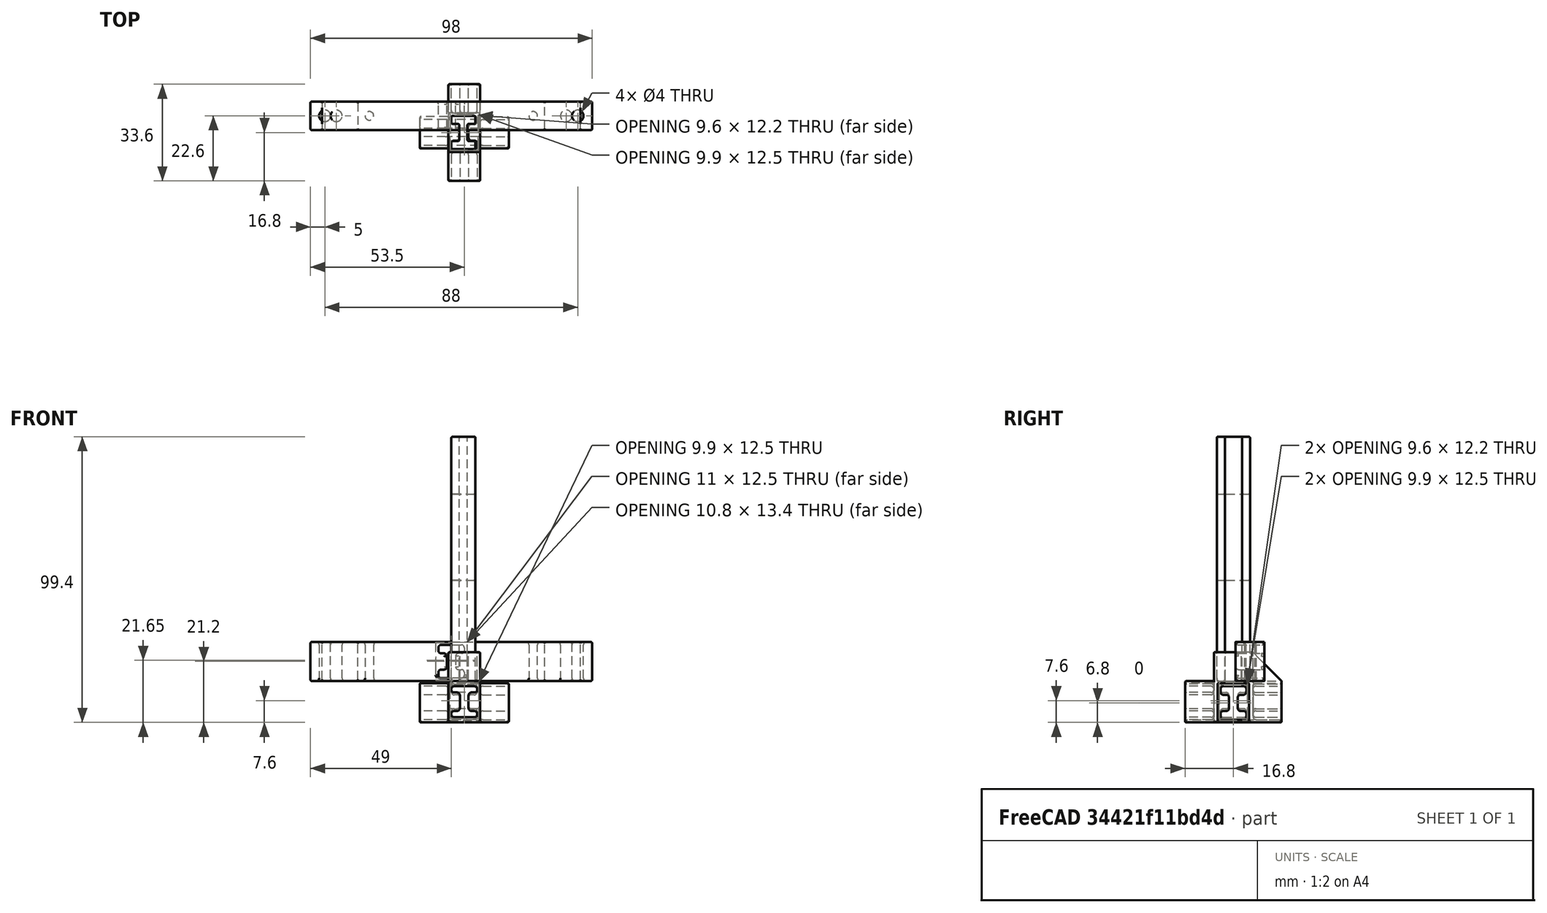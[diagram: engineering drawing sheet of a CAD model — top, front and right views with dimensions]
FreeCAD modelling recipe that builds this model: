
FCSTD DOCUMENT  (FreeCAD 1.2R20260106 (Git shallow))
Label: Joints
License: All rights reserved
LicenseURL: https://en.wikipedia.org/wiki/All_rights_reserved
objects: PartDesign::Fillet×30, Sketcher::SketchObject×28, PartDesign::Pad×25, App::Point×17, PartDesign::SubShapeBinder×10, PartDesign::Body×10, PartDesign::Pocket×6, PartDesign::Hole×3
note: 268 computed .brp shape members not serialized (recipe doc carries the construction recipe); baked Part::Feature solids carry a one-line shape summary decoded from their .brp

FEATURE [Sketcher::SketchObject] Sketch  label="MasterSketchConnector"
  ArcFitTolerance = 1e-06
  ExternalTypes = [0]
  FullyConstrained = true
  MakeInternals = false
  MapMode = 5
  expr: Constraints[20] = 3 * 3
  expr: Constraints[39] = 3 / 2
  expr: Constraints[79] = 2.8 * 2
  sketch-geometry (41):
    g0: LineSegment [constr] StartX=0 StartY=0 StartZ=0 EndX=0 EndY=-3 EndZ=0
    g1: LineSegment [constr] StartX=0 StartY=-3 StartZ=0 EndX=9 EndY=-3 EndZ=0
    g2: LineSegment [constr] StartX=9 StartY=-3 StartZ=0 EndX=9 EndY=0 EndZ=0
    g3: LineSegment [constr] StartX=9 StartY=0 StartZ=0 EndX=0 EndY=0 EndZ=0
    g4: GeomPoint [constr] X=4.5 Y=-1.5 Z=0
    g5: LineSegment [constr] StartX=0 StartY=-8.6 StartZ=0 EndX=0 EndY=-11.6 EndZ=0
    g6: LineSegment [constr] StartX=0 StartY=-11.6 StartZ=0 EndX=9 EndY=-11.6 EndZ=0
    g7: LineSegment [constr] StartX=9 StartY=-11.6 StartZ=0 EndX=9 EndY=-8.6 EndZ=0
    g8: LineSegment [constr] StartX=9 StartY=-8.6 StartZ=0 EndX=0 EndY=-8.6 EndZ=0
    g9: GeomPoint [constr] X=4.5 Y=-10.1 Z=0
    g10: LineSegment [constr] StartX=4.5 StartY=-1.5 StartZ=0 EndX=4.5 EndY=-10.1 EndZ=0
    g11: GeomPoint [constr] X=4.5 Y=-3 Z=0
    g12: GeomPoint [constr] X=4.5 Y=-8.6 Z=0
    g13: LineSegment [constr] StartX=4.5 StartY=-3 StartZ=0 EndX=4.5 EndY=-8.6 EndZ=0
    g14: LineSegment [constr] StartX=4.5 StartY=-8.6 StartZ=0 EndX=6 EndY=-8.6 EndZ=0
    g15: LineSegment [constr] StartX=6 StartY=-8.6 StartZ=0 EndX=6 EndY=-3 EndZ=0
    g16: LineSegment [constr] StartX=6 StartY=-3 StartZ=0 EndX=4.5 EndY=-3 EndZ=0
    g17: LineSegment [constr] StartX=4.5 StartY=-3 StartZ=0 EndX=3 EndY=-3 EndZ=0
    g18: LineSegment [constr] StartX=3 StartY=-3 StartZ=0 EndX=3 EndY=-8.6 EndZ=0
    g19: LineSegment [constr] StartX=3 StartY=-8.6 StartZ=0 EndX=4.5 EndY=-8.6 EndZ=0
    g20: LineSegment [constr] StartX=4.5 StartY=-8.6 StartZ=0 EndX=4.5 EndY=-3 EndZ=0
    g21: LineSegment [constr] StartX=0 StartY=0 StartZ=0 EndX=9 EndY=0 EndZ=0
    g22: LineSegment [constr] StartX=9 StartY=0 StartZ=0 EndX=9 EndY=-3 EndZ=0
    g23: LineSegment StartX=0 StartY=0 StartZ=0 EndX=9 EndY=0 EndZ=0
    g24: LineSegment StartX=9 StartY=0 StartZ=0 EndX=9 EndY=-3 EndZ=0
    g25: LineSegment StartX=9 StartY=-3 StartZ=0 EndX=6 EndY=-3 EndZ=0
    g26: LineSegment StartX=6 StartY=-3 StartZ=0 EndX=6 EndY=-8.6 EndZ=0
    g27: LineSegment StartX=6 StartY=-8.6 StartZ=0 EndX=9 EndY=-8.6 EndZ=0
    g28: LineSegment StartX=9 StartY=-8.6 StartZ=0 EndX=9 EndY=-11.6 EndZ=0
    g29: LineSegment StartX=9 StartY=-11.6 StartZ=0 EndX=0 EndY=-11.6 EndZ=0
    g30: LineSegment StartX=0 StartY=-11.6 StartZ=0 EndX=0 EndY=-8.6 EndZ=0
    g31: LineSegment StartX=0 StartY=-8.6 StartZ=0 EndX=3 EndY=-8.6 EndZ=0
    g32: LineSegment StartX=3 StartY=-8.6 StartZ=0 EndX=3 EndY=-3 EndZ=0
    g33: LineSegment StartX=3 StartY=-3 StartZ=0 EndX=0 EndY=-3 EndZ=0
    g34: LineSegment StartX=0 StartY=-3 StartZ=0 EndX=0 EndY=0 EndZ=0
    g35: GeomPoint X=4.5 Y=-5.8 Z=0
    g36: LineSegment StartX=-1 StartY=-12.6 StartZ=0 EndX=10 EndY=-12.6 EndZ=0
    g37: LineSegment StartX=10 StartY=-12.6 StartZ=0 EndX=10 EndY=1 EndZ=0
    g38: LineSegment StartX=10 StartY=1 StartZ=0 EndX=-1 EndY=1 EndZ=0
    g39: LineSegment StartX=-1 StartY=1 StartZ=0 EndX=-1 EndY=-12.6 EndZ=0
    g40: GeomPoint [constr] X=4.5 Y=-5.8 Z=0
  constraints (94):
    c: Coincident(g0,g1)
    c: Coincident(g1,g2)
    c: Coincident(g2,g3)
    c: Coincident(g3,g0)
    c: Vertical(g0)
    c: Vertical(g2)
    c: Horizontal(g1)
    c: Horizontal(g3)
    c: Symmetric(g0,g2,g4)
    c: Coincident(g5,g6)
    c: Coincident(g6,g7)
    c: Coincident(g7,g8)
    c: Coincident(g8,g5)
    c: Vertical(g5)
    c: Vertical(g7)
    c: Horizontal(g6)
    c: Horizontal(g8)
    c: Equal(g8,g1)
    c: Equal(g7,g2)
    c: Symmetric(g5,g7,g9)
    c: DistanceX(g3,g3) = 9
    c: DistanceY(g0,g0) = 3
    c: Coincident(g0,g-1)
    c: PointOnObject(g5,g-2)
    c: Coincident(g10,g4)
    c: Coincident(g10,g9)
    c: PointOnObject(g11,g10)
    c: PointOnObject(g12,g10)
    c: PointOnObject(g11,g1)
    c: PointOnObject(g12,g8)
    c: Coincident(g13,g14)
    c: Coincident(g14,g15)
    c: Coincident(g15,g16)
    c: Coincident(g16,g13)
    c: Vertical(g13)
    c: Vertical(g15)
    c: Horizontal(g14)
    c: Horizontal(g16)
    c: Coincident(g13,g11)
    c: Distance(g14,g14) = 1.5
    c: Coincident(g17,g18)
    c: Coincident(g18,g19)
    c: Coincident(g19,g20)
    c: Coincident(g20,g17)
    c: Horizontal(g17)
    c: Horizontal(g19)
    c: Vertical(g18)
    c: Vertical(g20)
    c: Coincident(g17,g11)
    c: Equal(g19,g14)
    c: PointOnObject(g12,g14)
    c: Coincident(g21,g0)
    c: Coincident(g21,g2)
    c: Coincident(g22,g2)
    c: Coincident(g22,g1)
    c: Coincident(g23,g0)
    c: Coincident(g23,g2)
    c: Coincident(g24,g2)
    c: Coincident(g24,g1)
    c: Coincident(g25,g1)
    c: Coincident(g25,g15)
    c: Coincident(g26,g15)
    c: Coincident(g26,g14)
    c: Coincident(g27,g14)
    c: Coincident(g27,g7)
    c: Coincident(g28,g7)
    c: Coincident(g28,g6)
    c: Coincident(g29,g6)
    c: Coincident(g29,g5)
    c: Coincident(g30,g5)
    c: Coincident(g30,g5)
    c: Coincident(g31,g5)
    c: Coincident(g31,g18)
    c: Coincident(g32,g18)
    c: Coincident(g32,g17)
    c: Coincident(g33,g17)
    c: Coincident(g33,g0)
    c: Coincident(g34,g0)
    c: Coincident(g34,g0)
    c: DistanceY(g15,g15) = 5.6
    c: Equal(g15,g18)
    c: Symmetric(g18,g15,g35)
    c: Coincident(g36,g37)
    c: Coincident(g37,g38)
    c: Coincident(g38,g39)
    c: Coincident(g39,g36)
    c: Horizontal(g36)
    c: Horizontal(g38)
    c: Vertical(g37)
    c: Vertical(g39)
    c: Symmetric(g38,g36,g40)
    c: Coincident(g40,g35)
    c: Distance(g38,g23) = 1
    c: Distance(g28,g37) = 1
FEATURE [App::Point] Origin003
  Role = Origin
FEATURE [PartDesign::SubShapeBinder] Binder001
  BindCopyOnChange = 0
  BindMode = 0
  ClaimChildren = false
  Context = -> Body001 [Binder001.]
  Fuse = false
  MakeFace = true
  OffsetFill = false
  OffsetIntersection = false
  OffsetJoinType = 0
  OffsetOpenResult = false
  PartialLoad = false
  Refine = true
  Relative = true
  Support = -> [Sketch]
  _Version = 2
FEATURE [PartDesign::Pad] Pad001  label="PadTopConnector"
  Direction = (0,0,1)
  Length = 10
  Length2 = 10
  Profile = -> Binder001 [Face1]
  Refine = true
  SideType = 0
  Suppressed = false
  Type = 0
  Type2 = 0
FEATURE [PartDesign::Pad] Pad002  label="PadBottom"
  BaseFeature = -> Pad001
  Direction = (0,0,1)
  Length = 14.4
  Length2 = 10
  Profile = -> Pad001 [Edge3,Edge11,Edge9,Edge6]
  Refine = true
  Reversed = true
  SideType = 0
  Suppressed = false
  Type = 0
  Type2 = 0
FEATURE [PartDesign::SubShapeBinder] Binder002  label="BinderFront"
  BindCopyOnChange = 0
  BindMode = 0
  ClaimChildren = false
  Context = -> Body001 [Binder002.Face1]
  Fuse = false
  MakeFace = true
  OffsetFill = false
  OffsetIntersection = false
  OffsetJoinType = 0
  OffsetOpenResult = false
  PartialLoad = false
  Placement = pos=(0,1,-1.8) rot=(1,0,0;1.5708rad)
  Refine = true
  Relative = true
  Support = -> [Sketch]
  _Version = 2
FEATURE [PartDesign::Pad] Pad003  label="PadRear"
  BaseFeature = -> Pad002
  Direction = (0,-1,2e-16)
  Length = 10
  Length2 = 10
  Profile = -> Binder002
  Refine = true
  Reversed = true
  SideType = 0
  Suppressed = false
  Type = 0
  Type2 = 0
FEATURE [Sketcher::SketchObject] Sketch001  label="SketchFront"
  ArcFitTolerance = 1e-06
  AttachmentSupport = -> [Pad003]
  ExternalGeometry = -> [Binder002]
  ExternalTypes = [0]
  FullyConstrained = true
  MakeInternals = false
  MapMode = 5
  Placement = pos=(0,-12.6,0) rot=(1,0,0;1.5708rad)
FEATURE [PartDesign::Pad] Pad004  label="PadFront"
  BaseFeature = -> Pad003
  Direction = (0,-1,2e-16)
  Length = 10
  Length2 = 10
  Profile = -> Sketch001
  ReferenceAxis = -> Sketch001 [N_Axis]
  Refine = true
  SideType = 0
  Suppressed = false
  Type = 0
  Type2 = 0
FEATURE [App::Point] Origin005  label="Origin006"
  Role = Origin
FEATURE [Sketcher::SketchObject] Sketch002  label="MasterSketchPole"
  ArcFitTolerance = 1e-06
  AttachmentSupport = -> [Origin004]
  ExternalTypes = [0]
  FullyConstrained = true
  MakeInternals = false
  MapMode = 5
  expr: Constraints[20] = 2.8 * 3
  expr: Constraints[39] = 2.8 / 2
  expr: Constraints[79] = 3 * 2
  sketch-geometry (37):
    g0: LineSegment [constr] StartX=0 StartY=0 StartZ=0 EndX=0 EndY=-2.8 EndZ=0
    g1: LineSegment [constr] StartX=0 StartY=-2.8 StartZ=0 EndX=8.4 EndY=-2.8 EndZ=0
    g2: LineSegment [constr] StartX=8.4 StartY=-2.8 StartZ=0 EndX=8.4 EndY=0 EndZ=0
    g3: LineSegment [constr] StartX=8.4 StartY=0 StartZ=0 EndX=0 EndY=0 EndZ=0
    g4: GeomPoint [constr] X=4.2 Y=-1.4 Z=0
    g5: LineSegment [constr] StartX=0 StartY=-8.8 StartZ=0 EndX=0 EndY=-11.6 EndZ=0
    g6: LineSegment [constr] StartX=0 StartY=-11.6 StartZ=0 EndX=8.4 EndY=-11.6 EndZ=0
    g7: LineSegment [constr] StartX=8.4 StartY=-11.6 StartZ=0 EndX=8.4 EndY=-8.8 EndZ=0
    g8: LineSegment [constr] StartX=8.4 StartY=-8.8 StartZ=0 EndX=0 EndY=-8.8 EndZ=0
    g9: GeomPoint [constr] X=4.2 Y=-10.2 Z=0
    g10: LineSegment [constr] StartX=4.2 StartY=-1.4 StartZ=0 EndX=4.2 EndY=-10.2 EndZ=0
    g11: GeomPoint [constr] X=4.2 Y=-2.8 Z=0
    g12: GeomPoint [constr] X=4.2 Y=-8.8 Z=0
    g13: LineSegment [constr] StartX=4.2 StartY=-2.8 StartZ=0 EndX=4.2 EndY=-8.8 EndZ=0
    g14: LineSegment [constr] StartX=4.2 StartY=-8.8 StartZ=0 EndX=5.6 EndY=-8.8 EndZ=0
    g15: LineSegment [constr] StartX=5.6 StartY=-8.8 StartZ=0 EndX=5.6 EndY=-2.8 EndZ=0
    g16: LineSegment [constr] StartX=5.6 StartY=-2.8 StartZ=0 EndX=4.2 EndY=-2.8 EndZ=0
    g17: LineSegment [constr] StartX=4.2 StartY=-2.8 StartZ=0 EndX=2.8 EndY=-2.8 EndZ=0
    g18: LineSegment [constr] StartX=2.8 StartY=-2.8 StartZ=0 EndX=2.8 EndY=-8.8 EndZ=0
    g19: LineSegment [constr] StartX=2.8 StartY=-8.8 StartZ=0 EndX=4.2 EndY=-8.8 EndZ=0
    g20: LineSegment [constr] StartX=4.2 StartY=-8.8 StartZ=0 EndX=4.2 EndY=-2.8 EndZ=0
    g21: LineSegment [constr] StartX=0 StartY=0 StartZ=0 EndX=8.4 EndY=0 EndZ=0
    g22: LineSegment [constr] StartX=8.4 StartY=0 StartZ=0 EndX=8.4 EndY=-2.8 EndZ=0
    g23: LineSegment StartX=0 StartY=0 StartZ=0 EndX=8.4 EndY=0 EndZ=0
    g24: LineSegment StartX=8.4 StartY=0 StartZ=0 EndX=8.4 EndY=-2.8 EndZ=0
    g25: LineSegment StartX=8.4 StartY=-2.8 StartZ=0 EndX=5.6 EndY=-2.8 EndZ=0
    g26: LineSegment StartX=5.6 StartY=-2.8 StartZ=0 EndX=5.6 EndY=-8.8 EndZ=0
    g27: LineSegment StartX=5.6 StartY=-8.8 StartZ=0 EndX=8.4 EndY=-8.8 EndZ=0
    g28: LineSegment StartX=8.4 StartY=-8.8 StartZ=0 EndX=8.4 EndY=-11.6 EndZ=0
    g29: LineSegment StartX=8.4 StartY=-11.6 StartZ=0 EndX=0 EndY=-11.6 EndZ=0
    g30: LineSegment StartX=0 StartY=-11.6 StartZ=0 EndX=0 EndY=-8.8 EndZ=0
    g31: LineSegment StartX=0 StartY=-8.8 StartZ=0 EndX=2.8 EndY=-8.8 EndZ=0
    g32: LineSegment StartX=2.8 StartY=-8.8 StartZ=0 EndX=2.8 EndY=-2.8 EndZ=0
    g33: LineSegment StartX=2.8 StartY=-2.8 StartZ=0 EndX=0 EndY=-2.8 EndZ=0
    g34: LineSegment StartX=0 StartY=-2.8 StartZ=0 EndX=0 EndY=0 EndZ=0
    g35: GeomPoint X=4.2 Y=-5.8 Z=0
    g36: GeomPoint [constr] X=4.2 Y=-5.8 Z=0
  constraints (83):
    c: Coincident(g0,g1)
    c: Coincident(g1,g2)
    c: Coincident(g2,g3)
    c: Coincident(g3,g0)
    c: Vertical(g0)
    c: Vertical(g2)
    c: Horizontal(g1)
    c: Horizontal(g3)
    c: Symmetric(g0,g2,g4)
    c: Coincident(g5,g6)
    c: Coincident(g6,g7)
    c: Coincident(g7,g8)
    c: Coincident(g8,g5)
    c: Vertical(g5)
    c: Vertical(g7)
    c: Horizontal(g6)
    c: Horizontal(g8)
    c: Equal(g8,g1)
    c: Equal(g7,g2)
    c: Symmetric(g5,g7,g9)
    c: DistanceX(g3,g3) = 8.4
    c: DistanceY(g0,g0) = 2.8
    c: Coincident(g0,g-1)
    c: PointOnObject(g5,g-2)
    c: Coincident(g10,g4)
    c: Coincident(g10,g9)
    c: PointOnObject(g11,g10)
    c: PointOnObject(g12,g10)
    c: PointOnObject(g11,g1)
    c: PointOnObject(g12,g8)
    c: Coincident(g13,g14)
    c: Coincident(g14,g15)
    c: Coincident(g15,g16)
    c: Coincident(g16,g13)
    c: Vertical(g13)
    c: Vertical(g15)
    c: Horizontal(g14)
    c: Horizontal(g16)
    c: Coincident(g13,g11)
    c: Distance(g14,g14) = 1.4
    c: Coincident(g17,g18)
    c: Coincident(g18,g19)
    c: Coincident(g19,g20)
    c: Coincident(g20,g17)
    c: Horizontal(g17)
    c: Horizontal(g19)
    c: Vertical(g18)
    c: Vertical(g20)
    c: Coincident(g17,g11)
    c: Equal(g19,g14)
    c: PointOnObject(g12,g14)
    c: Coincident(g21,g0)
    c: Coincident(g21,g2)
    c: Coincident(g22,g2)
    c: Coincident(g22,g1)
    c: Coincident(g23,g0)
    c: Coincident(g23,g2)
    c: Coincident(g24,g2)
    c: Coincident(g24,g1)
    c: Coincident(g25,g1)
    c: Coincident(g25,g15)
    c: Coincident(g26,g15)
    c: Coincident(g26,g14)
    c: Coincident(g27,g14)
    c: Coincident(g27,g7)
    c: Coincident(g28,g7)
    c: Coincident(g28,g6)
    c: Coincident(g29,g6)
    c: Coincident(g29,g5)
    c: Coincident(g30,g5)
    c: Coincident(g30,g5)
    c: Coincident(g31,g5)
    c: Coincident(g31,g18)
    c: Coincident(g32,g18)
    c: Coincident(g32,g17)
    c: Coincident(g33,g17)
    c: Coincident(g33,g0)
    c: Coincident(g34,g0)
    c: Coincident(g34,g0)
    c: DistanceY(g15,g15) = 6
    c: Equal(g15,g18)
    c: Symmetric(g18,g15,g35)
    c: Coincident(g36,g35)
FEATURE [PartDesign::SubShapeBinder] Binder  label="BinderFront001"
  BindCopyOnChange = 0
  BindMode = 0
  ClaimChildren = false
  Context = -> Body001 [Binder.]
  Fuse = false
  MakeFace = true
  OffsetFill = false
  OffsetIntersection = false
  OffsetJoinType = 0
  OffsetOpenResult = false
  PartialLoad = false
  Placement = pos=(0,-100,0) rot=(0.57735,0.57735,0.57735;2.0944rad)
  Refine = true
  Relative = true
  Support = -> [Sketch]
  _Version = 2
FEATURE [Sketcher::SketchObject] Sketch003  label="SketchLeft"
  ArcFitTolerance = 1e-06
  AttachmentSupport = -> [Pad004]
  ExternalGeometry = -> [Pad004,Binder]
  ExternalTypes = [0,0]
  FullyConstrained = true
  MakeInternals = false
  MapMode = 5
  Placement = pos=(-1,0,0) rot=(0.57735,-0.57735,-0.57735;2.0944rad)
  sketch-geometry (22):
    g0: LineSegment StartX=1.3 StartY=-4.8 StartZ=0 EndX=1.3 EndY=-1.8 EndZ=0
    g1: LineSegment StartX=4.3 StartY=-4.8 StartZ=0 EndX=1.3 EndY=-4.8 EndZ=0
    g2: LineSegment StartX=4.3 StartY=-10.4 StartZ=0 EndX=4.3 EndY=-4.8 EndZ=0
    g3: LineSegment StartX=1.3 StartY=-10.4 StartZ=0 EndX=4.3 EndY=-10.4 EndZ=0
    g4: LineSegment StartX=1.3 StartY=-13.4 StartZ=0 EndX=1.3 EndY=-10.4 EndZ=0
    g5: LineSegment StartX=10.3 StartY=-13.4 StartZ=0 EndX=1.3 EndY=-13.4 EndZ=0
    g6: LineSegment StartX=10.3 StartY=-10.4 StartZ=0 EndX=10.3 EndY=-13.4 EndZ=0
    g7: LineSegment StartX=7.3 StartY=-10.4 StartZ=0 EndX=10.3 EndY=-10.4 EndZ=0
    g8: LineSegment StartX=7.3 StartY=-4.8 StartZ=0 EndX=7.3 EndY=-10.4 EndZ=0
    g9: LineSegment StartX=10.3 StartY=-4.8 StartZ=0 EndX=7.3 EndY=-4.8 EndZ=0
    g10: LineSegment StartX=10.3 StartY=-1.8 StartZ=0 EndX=10.3 EndY=-4.8 EndZ=0
    g11: LineSegment StartX=1.3 StartY=-1.8 StartZ=0 EndX=10.3 EndY=-1.8 EndZ=0
    g12: LineSegment StartX=11.3 StartY=-0.8 StartZ=0 EndX=11.3 EndY=-14.4 EndZ=0
    g13: LineSegment StartX=0.3 StartY=-0.8 StartZ=0 EndX=11.3 EndY=-0.8 EndZ=0
    g14: LineSegment StartX=0.3 StartY=-14.4 StartZ=0 EndX=0.3 EndY=-0.8 EndZ=0
    g15: LineSegment StartX=11.3 StartY=-14.4 StartZ=0 EndX=0.3 EndY=-14.4 EndZ=0
    g16: GeomPoint [constr] X=5.8 Y=-7.6 Z=0
    g17: GeomPoint [constr] X=5.8 Y=-7.6 Z=0
    g18: LineSegment [constr] StartX=5.8 StartY=-7.6 StartZ=0 EndX=5.8 EndY=-14.4 EndZ=0
    g19: LineSegment [constr] StartX=-1 StartY=-0.8 StartZ=0 EndX=-1 EndY=-14.4 EndZ=0
    g20: GeomPoint [constr] X=5.8 Y=-7.6 Z=0
    g21: LineSegment [constr] StartX=5.8 StartY=-7.6 StartZ=0 EndX=5.8 EndY=-14.4 EndZ=0
  constraints (56):
    c: Coincident(g13,g14)
    c: Coincident(g12,g13)
    c: Coincident(g12,g15)
    c: Coincident(g15,g14)
    c: Coincident(g6,g7)
    c: Coincident(g5,g6)
    c: Coincident(g7,g8)
    c: Coincident(g8,g9)
    c: Coincident(g9,g10)
    c: Coincident(g10,g11)
    c: Coincident(g0,g11)
    c: Coincident(g0,g1)
    c: Coincident(g1,g2)
    c: Coincident(g2,g3)
    c: Coincident(g3,g4)
    c: Coincident(g4,g5)
    c: Equal(g14,g12)
    c: Equal(g13,g15)
    c: Equal(g0,g4)
    c: Equal(g4,g6)
    c: Equal(g6,g10)
    c: Equal(g8,g2)
    c: Equal(g9,g1)
    c: Equal(g1,g3)
    c: Equal(g3,g7)
    c: Horizontal(g13)
    c: Horizontal(g11)
    c: Horizontal(g1)
    c: Horizontal(g9)
    c: Horizontal(g7)
    c: Horizontal(g3)
    c: Horizontal(g5)
    c: Vertical(g12)
    c: Vertical(g10)
    c: Vertical(g0)
    c: Vertical(g2)
    c: Vertical(g8)
    c: Vertical(g4)
    c: Symmetric(g12,g13,g16)
    c: Symmetric(g4,g10,g17)
    c: Coincident(g16,g17)
    c: Coincident(g18,g16)
    c: Symmetric(g15,g15,g18)
    c: Coincident(g19,g-4)
    c: PointOnObject(g19,g-6)
    c: Vertical(g19)
    c: Symmetric(g19,g-9,g20)
    c: Coincident(g21,g20)
    c: Symmetric(g-6,g-6,g21)
    c: Equal(g13,g-13)
    c: Equal(g10,g-16)
    c: Equal(g11,g-15)
    c: Equal(g8,g-18)
    c: Equal(g9,g-17)
    c: Equal(g12,g-12)
    c: Coincident(g18,g21)
FEATURE [PartDesign::Pad] Pad006  label="PadLeft"
  BaseFeature = -> Pad004
  Direction = (-1,0,0)
  Length = 10
  Length2 = 10
  Profile = -> Sketch003
  ReferenceAxis = -> Sketch003 [N_Axis]
  Refine = true
  SideType = 0
  Suppressed = false
  Type = 0
  Type2 = 0
FEATURE [Sketcher::SketchObject] Sketch004  label="SketchRight"
  ArcFitTolerance = 1e-06
  AttachmentSupport = -> [Pad006]
  ExternalGeometry = -> [Sketch003]
  ExternalTypes = [0,0,0,0,0,0,0,0,0,0,0,0,0,0,0,0]
  FullyConstrained = true
  MakeInternals = false
  MapMode = 5
  Placement = pos=(10,0,0) rot=(0.57735,0.57735,0.57735;2.0944rad)
FEATURE [PartDesign::Pad] Pad007  label="PadRight"
  BaseFeature = -> Pad006
  Direction = (1,0,0)
  Length = 10
  Length2 = 10
  Profile = -> Sketch004
  ReferenceAxis = -> Sketch004 [N_Axis]
  Refine = true
  SideType = 0
  Suppressed = false
  Type = 0
  Type2 = 0
FEATURE [PartDesign::Fillet] Fillet001  label="FilletInside"
  Base = -> Pad007 [Edge182,Edge184,Edge186,Edge202,Edge188,Edge181,Edge190,Edge200,Edge192,Edge198,Edge196,Edge194,Edge107,Edge108,Edge110,Edge128,Edge126,Edge112,Edge114,Edge124,Edge122,Edge116,Edge118,Edge120,Edge226,Edge205,Edge206,Edge224,Edge222,Edge208,Edge220,Edge210,Edge218,Edge216,Edge214,Edge212,Edge144,Edge145,Edge149,Edge165,+20 more]
  BaseFeature = -> Pad007
  Radius = 1
  Refine = true
  SupportTransform = false
  Suppressed = false
  UseAllEdges = false
FEATURE [PartDesign::Fillet] Fillet002  label="FilletBottom"
  Base = -> Fillet001 [Face34]
  BaseFeature = -> Fillet001
  Radius = 0.5
  Refine = true
  SupportTransform = false
  Suppressed = false
  UseAllEdges = false
FEATURE [PartDesign::Fillet] Fillet003  label="FilletAroundJointEdge"
  Base = -> Fillet002 [Edge79,Edge51,Edge47,Edge1,Edge14,Edge15,Edge309,Edge307,Edge305,Edge88,Edge86,Edge12,Edge76,Edge7,Edge48,Edge77]
  BaseFeature = -> Fillet002
  Radius = 0.3
  Refine = true
  SupportTransform = false
  Suppressed = false
  UseAllEdges = false
FEATURE [PartDesign::Fillet] Fillet004  label="FilletEverythingElse"
  Base = -> Fillet003 [Edge253,Edge92,Edge254,Edge37,Edge44,Edge39,Edge12,Edge10,Edge7,Edge5,Edge23,Edge6,Edge4,Edge3,Edge21,Edge26,Edge91,Edge93,Edge24,Edge27]
  BaseFeature = -> Fillet003
  Radius = 0.25
  Refine = true
  SupportTransform = false
  Suppressed = false
  UseAllEdges = false
FEATURE [App::Point] Origin007  label="Origin008"
  Role = Origin
FEATURE [Sketcher::SketchObject] Sketch005  label="MasterSketchConnector001"
  ArcFitTolerance = 1e-06
  AttachmentSupport = -> [Origin006]
  ExternalTypes = [0]
  FullyConstrained = true
  MakeInternals = false
  MapMode = 5
  expr: Constraints[20] = 3 * 3
  expr: Constraints[39] = 3 / 2
  expr: Constraints[79] = 2.8 * 2
  sketch-geometry (41):
    g0: LineSegment [constr] StartX=0 StartY=0 StartZ=0 EndX=0 EndY=-3 EndZ=0
    g1: LineSegment [constr] StartX=0 StartY=-3 StartZ=0 EndX=9 EndY=-3 EndZ=0
    g2: LineSegment [constr] StartX=9 StartY=-3 StartZ=0 EndX=9 EndY=0 EndZ=0
    g3: LineSegment [constr] StartX=9 StartY=0 StartZ=0 EndX=0 EndY=0 EndZ=0
    g4: GeomPoint [constr] X=4.5 Y=-1.5 Z=0
    g5: LineSegment [constr] StartX=0 StartY=-8.6 StartZ=0 EndX=0 EndY=-11.6 EndZ=0
    g6: LineSegment [constr] StartX=0 StartY=-11.6 StartZ=0 EndX=9 EndY=-11.6 EndZ=0
    g7: LineSegment [constr] StartX=9 StartY=-11.6 StartZ=0 EndX=9 EndY=-8.6 EndZ=0
    g8: LineSegment [constr] StartX=9 StartY=-8.6 StartZ=0 EndX=0 EndY=-8.6 EndZ=0
    g9: GeomPoint [constr] X=4.5 Y=-10.1 Z=0
    g10: LineSegment [constr] StartX=4.5 StartY=-1.5 StartZ=0 EndX=4.5 EndY=-10.1 EndZ=0
    g11: GeomPoint [constr] X=4.5 Y=-3 Z=0
    g12: GeomPoint [constr] X=4.5 Y=-8.6 Z=0
    g13: LineSegment [constr] StartX=4.5 StartY=-3 StartZ=0 EndX=4.5 EndY=-8.6 EndZ=0
    g14: LineSegment [constr] StartX=4.5 StartY=-8.6 StartZ=0 EndX=6 EndY=-8.6 EndZ=0
    g15: LineSegment [constr] StartX=6 StartY=-8.6 StartZ=0 EndX=6 EndY=-3 EndZ=0
    g16: LineSegment [constr] StartX=6 StartY=-3 StartZ=0 EndX=4.5 EndY=-3 EndZ=0
    g17: LineSegment [constr] StartX=4.5 StartY=-3 StartZ=0 EndX=3 EndY=-3 EndZ=0
    g18: LineSegment [constr] StartX=3 StartY=-3 StartZ=0 EndX=3 EndY=-8.6 EndZ=0
    g19: LineSegment [constr] StartX=3 StartY=-8.6 StartZ=0 EndX=4.5 EndY=-8.6 EndZ=0
    g20: LineSegment [constr] StartX=4.5 StartY=-8.6 StartZ=0 EndX=4.5 EndY=-3 EndZ=0
    g21: LineSegment [constr] StartX=0 StartY=0 StartZ=0 EndX=9 EndY=0 EndZ=0
    g22: LineSegment [constr] StartX=9 StartY=0 StartZ=0 EndX=9 EndY=-3 EndZ=0
    g23: LineSegment StartX=0 StartY=0 StartZ=0 EndX=9 EndY=0 EndZ=0
    g24: LineSegment StartX=9 StartY=0 StartZ=0 EndX=9 EndY=-3 EndZ=0
    g25: LineSegment StartX=9 StartY=-3 StartZ=0 EndX=6 EndY=-3 EndZ=0
    g26: LineSegment StartX=6 StartY=-3 StartZ=0 EndX=6 EndY=-8.6 EndZ=0
    g27: LineSegment StartX=6 StartY=-8.6 StartZ=0 EndX=9 EndY=-8.6 EndZ=0
    g28: LineSegment StartX=9 StartY=-8.6 StartZ=0 EndX=9 EndY=-11.6 EndZ=0
    g29: LineSegment StartX=9 StartY=-11.6 StartZ=0 EndX=0 EndY=-11.6 EndZ=0
    g30: LineSegment StartX=0 StartY=-11.6 StartZ=0 EndX=0 EndY=-8.6 EndZ=0
    g31: LineSegment StartX=0 StartY=-8.6 StartZ=0 EndX=3 EndY=-8.6 EndZ=0
    g32: LineSegment StartX=3 StartY=-8.6 StartZ=0 EndX=3 EndY=-3 EndZ=0
    g33: LineSegment StartX=3 StartY=-3 StartZ=0 EndX=0 EndY=-3 EndZ=0
    g34: LineSegment StartX=0 StartY=-3 StartZ=0 EndX=0 EndY=0 EndZ=0
    g35: GeomPoint X=4.5 Y=-5.8 Z=0
    g36: LineSegment StartX=-1 StartY=-12.6 StartZ=0 EndX=10 EndY=-12.6 EndZ=0
    g37: LineSegment StartX=10 StartY=-12.6 StartZ=0 EndX=10 EndY=1 EndZ=0
    g38: LineSegment StartX=10 StartY=1 StartZ=0 EndX=-1 EndY=1 EndZ=0
    g39: LineSegment StartX=-1 StartY=1 StartZ=0 EndX=-1 EndY=-12.6 EndZ=0
    g40: GeomPoint [constr] X=4.5 Y=-5.8 Z=0
  constraints (94):
    c: Coincident(g0,g1)
    c: Coincident(g1,g2)
    c: Coincident(g2,g3)
    c: Coincident(g3,g0)
    c: Vertical(g0)
    c: Vertical(g2)
    c: Horizontal(g1)
    c: Horizontal(g3)
    c: Symmetric(g0,g2,g4)
    c: Coincident(g5,g6)
    c: Coincident(g6,g7)
    c: Coincident(g7,g8)
    c: Coincident(g8,g5)
    c: Vertical(g5)
    c: Vertical(g7)
    c: Horizontal(g6)
    c: Horizontal(g8)
    c: Equal(g8,g1)
    c: Equal(g7,g2)
    c: Symmetric(g5,g7,g9)
    c: DistanceX(g3,g3) = 9
    c: DistanceY(g0,g0) = 3
    c: Coincident(g0,g-1)
    c: PointOnObject(g5,g-2)
    c: Coincident(g10,g4)
    c: Coincident(g10,g9)
    c: PointOnObject(g11,g10)
    c: PointOnObject(g12,g10)
    c: PointOnObject(g11,g1)
    c: PointOnObject(g12,g8)
    c: Coincident(g13,g14)
    c: Coincident(g14,g15)
    c: Coincident(g15,g16)
    c: Coincident(g16,g13)
    c: Vertical(g13)
    c: Vertical(g15)
    c: Horizontal(g14)
    c: Horizontal(g16)
    c: Coincident(g13,g11)
    c: Distance(g14,g14) = 1.5
    c: Coincident(g17,g18)
    c: Coincident(g18,g19)
    c: Coincident(g19,g20)
    c: Coincident(g20,g17)
    c: Horizontal(g17)
    c: Horizontal(g19)
    c: Vertical(g18)
    c: Vertical(g20)
    c: Coincident(g17,g11)
    c: Equal(g19,g14)
    c: PointOnObject(g12,g14)
    c: Coincident(g21,g0)
    c: Coincident(g21,g2)
    c: Coincident(g22,g2)
    c: Coincident(g22,g1)
    c: Coincident(g23,g0)
    c: Coincident(g23,g2)
    c: Coincident(g24,g2)
    c: Coincident(g24,g1)
    c: Coincident(g25,g1)
    c: Coincident(g25,g15)
    c: Coincident(g26,g15)
    c: Coincident(g26,g14)
    c: Coincident(g27,g14)
    c: Coincident(g27,g7)
    c: Coincident(g28,g7)
    c: Coincident(g28,g6)
    c: Coincident(g29,g6)
    c: Coincident(g29,g5)
    c: Coincident(g30,g5)
    c: Coincident(g30,g5)
    c: Coincident(g31,g5)
    c: Coincident(g31,g18)
    c: Coincident(g32,g18)
    c: Coincident(g32,g17)
    c: Coincident(g33,g17)
    c: Coincident(g33,g0)
    c: Coincident(g34,g0)
    c: Coincident(g34,g0)
    c: DistanceY(g15,g15) = 5.6
    c: Equal(g15,g18)
    c: Symmetric(g18,g15,g35)
    c: Coincident(g36,g37)
    c: Coincident(g37,g38)
    c: Coincident(g38,g39)
    c: Coincident(g39,g36)
    c: Horizontal(g36)
    c: Horizontal(g38)
    c: Vertical(g37)
    c: Vertical(g39)
    c: Symmetric(g38,g36,g40)
    c: Coincident(g40,g35)
    c: Distance(g38,g23) = 1
    c: Distance(g28,g37) = 1
FEATURE [App::Point] Origin009  label="Origin010"
  Role = Origin
FEATURE [Sketcher::SketchObject] Sketch006  label="MasterSketchConnector002"
  ArcFitTolerance = 1e-06
  AttachmentSupport = -> [Origin008]
  ExternalTypes = [0]
  FullyConstrained = true
  MakeInternals = false
  MapMode = 5
  expr: Constraints[20] = 3 * 3
  expr: Constraints[39] = 3 / 2
  expr: Constraints[79] = 2.8 * 2
  sketch-geometry (41):
    g0: LineSegment [constr] StartX=0 StartY=0 StartZ=0 EndX=0 EndY=-3 EndZ=0
    g1: LineSegment [constr] StartX=0 StartY=-3 StartZ=0 EndX=9 EndY=-3 EndZ=0
    g2: LineSegment [constr] StartX=9 StartY=-3 StartZ=0 EndX=9 EndY=0 EndZ=0
    g3: LineSegment [constr] StartX=9 StartY=0 StartZ=0 EndX=0 EndY=0 EndZ=0
    g4: GeomPoint [constr] X=4.5 Y=-1.5 Z=0
    g5: LineSegment [constr] StartX=0 StartY=-8.6 StartZ=0 EndX=0 EndY=-11.6 EndZ=0
    g6: LineSegment [constr] StartX=0 StartY=-11.6 StartZ=0 EndX=9 EndY=-11.6 EndZ=0
    g7: LineSegment [constr] StartX=9 StartY=-11.6 StartZ=0 EndX=9 EndY=-8.6 EndZ=0
    g8: LineSegment [constr] StartX=9 StartY=-8.6 StartZ=0 EndX=0 EndY=-8.6 EndZ=0
    g9: GeomPoint [constr] X=4.5 Y=-10.1 Z=0
    g10: LineSegment [constr] StartX=4.5 StartY=-1.5 StartZ=0 EndX=4.5 EndY=-10.1 EndZ=0
    g11: GeomPoint [constr] X=4.5 Y=-3 Z=0
    g12: GeomPoint [constr] X=4.5 Y=-8.6 Z=0
    g13: LineSegment [constr] StartX=4.5 StartY=-3 StartZ=0 EndX=4.5 EndY=-8.6 EndZ=0
    g14: LineSegment [constr] StartX=4.5 StartY=-8.6 StartZ=0 EndX=6 EndY=-8.6 EndZ=0
    g15: LineSegment [constr] StartX=6 StartY=-8.6 StartZ=0 EndX=6 EndY=-3 EndZ=0
    g16: LineSegment [constr] StartX=6 StartY=-3 StartZ=0 EndX=4.5 EndY=-3 EndZ=0
    g17: LineSegment [constr] StartX=4.5 StartY=-3 StartZ=0 EndX=3 EndY=-3 EndZ=0
    g18: LineSegment [constr] StartX=3 StartY=-3 StartZ=0 EndX=3 EndY=-8.6 EndZ=0
    g19: LineSegment [constr] StartX=3 StartY=-8.6 StartZ=0 EndX=4.5 EndY=-8.6 EndZ=0
    g20: LineSegment [constr] StartX=4.5 StartY=-8.6 StartZ=0 EndX=4.5 EndY=-3 EndZ=0
    g21: LineSegment [constr] StartX=0 StartY=0 StartZ=0 EndX=9 EndY=0 EndZ=0
    g22: LineSegment [constr] StartX=9 StartY=0 StartZ=0 EndX=9 EndY=-3 EndZ=0
    g23: LineSegment StartX=0 StartY=0 StartZ=0 EndX=9 EndY=0 EndZ=0
    g24: LineSegment StartX=9 StartY=0 StartZ=0 EndX=9 EndY=-3 EndZ=0
    g25: LineSegment StartX=9 StartY=-3 StartZ=0 EndX=6 EndY=-3 EndZ=0
    g26: LineSegment StartX=6 StartY=-3 StartZ=0 EndX=6 EndY=-8.6 EndZ=0
    g27: LineSegment StartX=6 StartY=-8.6 StartZ=0 EndX=9 EndY=-8.6 EndZ=0
    g28: LineSegment StartX=9 StartY=-8.6 StartZ=0 EndX=9 EndY=-11.6 EndZ=0
    g29: LineSegment StartX=9 StartY=-11.6 StartZ=0 EndX=0 EndY=-11.6 EndZ=0
    g30: LineSegment StartX=0 StartY=-11.6 StartZ=0 EndX=0 EndY=-8.6 EndZ=0
    g31: LineSegment StartX=0 StartY=-8.6 StartZ=0 EndX=3 EndY=-8.6 EndZ=0
    g32: LineSegment StartX=3 StartY=-8.6 StartZ=0 EndX=3 EndY=-3 EndZ=0
    g33: LineSegment StartX=3 StartY=-3 StartZ=0 EndX=0 EndY=-3 EndZ=0
    g34: LineSegment StartX=0 StartY=-3 StartZ=0 EndX=0 EndY=0 EndZ=0
    g35: GeomPoint X=4.5 Y=-5.8 Z=0
    g36: LineSegment StartX=-1 StartY=-12.6 StartZ=0 EndX=10 EndY=-12.6 EndZ=0
    g37: LineSegment StartX=10 StartY=-12.6 StartZ=0 EndX=10 EndY=1 EndZ=0
    g38: LineSegment StartX=10 StartY=1 StartZ=0 EndX=-1 EndY=1 EndZ=0
    g39: LineSegment StartX=-1 StartY=1 StartZ=0 EndX=-1 EndY=-12.6 EndZ=0
    g40: GeomPoint [constr] X=4.5 Y=-5.8 Z=0
  constraints (94):
    c: Coincident(g0,g1)
    c: Coincident(g1,g2)
    c: Coincident(g2,g3)
    c: Coincident(g3,g0)
    c: Vertical(g0)
    c: Vertical(g2)
    c: Horizontal(g1)
    c: Horizontal(g3)
    c: Symmetric(g0,g2,g4)
    c: Coincident(g5,g6)
    c: Coincident(g6,g7)
    c: Coincident(g7,g8)
    c: Coincident(g8,g5)
    c: Vertical(g5)
    c: Vertical(g7)
    c: Horizontal(g6)
    c: Horizontal(g8)
    c: Equal(g8,g1)
    c: Equal(g7,g2)
    c: Symmetric(g5,g7,g9)
    c: DistanceX(g3,g3) = 9
    c: DistanceY(g0,g0) = 3
    c: Coincident(g0,g-1)
    c: PointOnObject(g5,g-2)
    c: Coincident(g10,g4)
    c: Coincident(g10,g9)
    c: PointOnObject(g11,g10)
    c: PointOnObject(g12,g10)
    c: PointOnObject(g11,g1)
    c: PointOnObject(g12,g8)
    c: Coincident(g13,g14)
    c: Coincident(g14,g15)
    c: Coincident(g15,g16)
    c: Coincident(g16,g13)
    c: Vertical(g13)
    c: Vertical(g15)
    c: Horizontal(g14)
    c: Horizontal(g16)
    c: Coincident(g13,g11)
    c: Distance(g14,g14) = 1.5
    c: Coincident(g17,g18)
    c: Coincident(g18,g19)
    c: Coincident(g19,g20)
    c: Coincident(g20,g17)
    c: Horizontal(g17)
    c: Horizontal(g19)
    c: Vertical(g18)
    c: Vertical(g20)
    c: Coincident(g17,g11)
    c: Equal(g19,g14)
    c: PointOnObject(g12,g14)
    c: Coincident(g21,g0)
    c: Coincident(g21,g2)
    c: Coincident(g22,g2)
    c: Coincident(g22,g1)
    c: Coincident(g23,g0)
    c: Coincident(g23,g2)
    c: Coincident(g24,g2)
    c: Coincident(g24,g1)
    c: Coincident(g25,g1)
    c: Coincident(g25,g15)
    c: Coincident(g26,g15)
    c: Coincident(g26,g14)
    c: Coincident(g27,g14)
    c: Coincident(g27,g7)
    c: Coincident(g28,g7)
    c: Coincident(g28,g6)
    c: Coincident(g29,g6)
    c: Coincident(g29,g5)
    c: Coincident(g30,g5)
    c: Coincident(g30,g5)
    c: Coincident(g31,g5)
    c: Coincident(g31,g18)
    c: Coincident(g32,g18)
    c: Coincident(g32,g17)
    c: Coincident(g33,g17)
    c: Coincident(g33,g0)
    c: Coincident(g34,g0)
    c: Coincident(g34,g0)
    c: DistanceY(g15,g15) = 5.6
    c: Equal(g15,g18)
    c: Symmetric(g18,g15,g35)
    c: Coincident(g36,g37)
    c: Coincident(g37,g38)
    c: Coincident(g38,g39)
    c: Coincident(g39,g36)
    c: Horizontal(g36)
    c: Horizontal(g38)
    c: Vertical(g37)
    c: Vertical(g39)
    c: Symmetric(g38,g36,g40)
    c: Coincident(g40,g35)
    c: Distance(g38,g23) = 1
    c: Distance(g28,g37) = 1
FEATURE [PartDesign::Fillet] Fillet009  label="FilletAroundJointEdgeAgain"
  Base = -> Fillet004 [Face23,Face147,Face34,Face38,Face151]
  BaseFeature = -> Fillet004
  Radius = 0.3
  Refine = true
  SupportTransform = false
  Suppressed = false
  UseAllEdges = false
FEATURE [PartDesign::SubShapeBinder] Binder006
  BindCopyOnChange = 0
  BindMode = 0
  ClaimChildren = false
  Context = -> Body002 [Binder006.]
  Fuse = false
  MakeFace = true
  OffsetFill = false
  OffsetIntersection = false
  OffsetJoinType = 0
  OffsetOpenResult = false
  PartialLoad = false
  Refine = true
  Relative = true
  Support = -> [Sketch007]
  _Version = 2
FEATURE [PartDesign::SubShapeBinder] Binder007  label="BinderFront003"
  BindCopyOnChange = 0
  BindMode = 0
  ClaimChildren = false
  Context = -> Body002 [Binder007.Face1]
  Fuse = false
  MakeFace = true
  OffsetFill = false
  OffsetIntersection = false
  OffsetJoinType = 0
  OffsetOpenResult = false
  PartialLoad = false
  Placement = pos=(0,1,-1.8) rot=(1,0,0;1.5708rad)
  Refine = true
  Relative = true
  Support = -> [Sketch007]
  _Version = 2
FEATURE [App::Point] Origin011  label="Origin012"
  Role = Origin
FEATURE [App::Point] Origin013  label="Origin014"
  Role = Origin
FEATURE [PartDesign::Pad] Pad008  label="PadTopConnector001"
  Direction = (0,0,1)
  Length = 10
  Length2 = 10
  Profile = -> Binder006 [Face1]
  Refine = true
  SideType = 0
  Suppressed = false
  Type = 0
  Type2 = 0
FEATURE [PartDesign::Pad] Pad009  label="PadBottom001"
  BaseFeature = -> Pad008
  Direction = (0,0,1)
  Length = 14.4
  Length2 = 10
  Profile = -> Pad008 [Edge3,Edge11,Edge9,Edge6]
  Refine = true
  Reversed = true
  SideType = 0
  Suppressed = false
  Type = 0
  Type2 = 0
FEATURE [PartDesign::Pad] Pad010  label="PadRear001"
  BaseFeature = -> Pad009
  Direction = (0,-1,2e-16)
  Length = 10
  Length2 = 10
  Profile = -> Binder007
  Refine = true
  Reversed = true
  SideType = 0
  Suppressed = false
  Type = 0
  Type2 = 0
FEATURE [Sketcher::SketchObject] Sketch007  label="MasterSketchConnector003"
  ArcFitTolerance = 1e-06
  AttachmentSupport = -> [Origin010]
  ExternalTypes = [0]
  FullyConstrained = true
  MakeInternals = false
  MapMode = 5
  expr: Constraints[20] = 3 * 3
  expr: Constraints[39] = 3 / 2
  expr: Constraints[79] = 2.8 * 2
  sketch-geometry (41):
    g0: LineSegment [constr] StartX=0 StartY=0 StartZ=0 EndX=0 EndY=-3 EndZ=0
    g1: LineSegment [constr] StartX=0 StartY=-3 StartZ=0 EndX=9 EndY=-3 EndZ=0
    g2: LineSegment [constr] StartX=9 StartY=-3 StartZ=0 EndX=9 EndY=0 EndZ=0
    g3: LineSegment [constr] StartX=9 StartY=0 StartZ=0 EndX=0 EndY=0 EndZ=0
    g4: GeomPoint [constr] X=4.5 Y=-1.5 Z=0
    g5: LineSegment [constr] StartX=0 StartY=-8.6 StartZ=0 EndX=0 EndY=-11.6 EndZ=0
    g6: LineSegment [constr] StartX=0 StartY=-11.6 StartZ=0 EndX=9 EndY=-11.6 EndZ=0
    g7: LineSegment [constr] StartX=9 StartY=-11.6 StartZ=0 EndX=9 EndY=-8.6 EndZ=0
    g8: LineSegment [constr] StartX=9 StartY=-8.6 StartZ=0 EndX=0 EndY=-8.6 EndZ=0
    g9: GeomPoint [constr] X=4.5 Y=-10.1 Z=0
    g10: LineSegment [constr] StartX=4.5 StartY=-1.5 StartZ=0 EndX=4.5 EndY=-10.1 EndZ=0
    g11: GeomPoint [constr] X=4.5 Y=-3 Z=0
    g12: GeomPoint [constr] X=4.5 Y=-8.6 Z=0
    g13: LineSegment [constr] StartX=4.5 StartY=-3 StartZ=0 EndX=4.5 EndY=-8.6 EndZ=0
    g14: LineSegment [constr] StartX=4.5 StartY=-8.6 StartZ=0 EndX=6 EndY=-8.6 EndZ=0
    g15: LineSegment [constr] StartX=6 StartY=-8.6 StartZ=0 EndX=6 EndY=-3 EndZ=0
    g16: LineSegment [constr] StartX=6 StartY=-3 StartZ=0 EndX=4.5 EndY=-3 EndZ=0
    g17: LineSegment [constr] StartX=4.5 StartY=-3 StartZ=0 EndX=3 EndY=-3 EndZ=0
    g18: LineSegment [constr] StartX=3 StartY=-3 StartZ=0 EndX=3 EndY=-8.6 EndZ=0
    g19: LineSegment [constr] StartX=3 StartY=-8.6 StartZ=0 EndX=4.5 EndY=-8.6 EndZ=0
    g20: LineSegment [constr] StartX=4.5 StartY=-8.6 StartZ=0 EndX=4.5 EndY=-3 EndZ=0
    g21: LineSegment [constr] StartX=0 StartY=0 StartZ=0 EndX=9 EndY=0 EndZ=0
    g22: LineSegment [constr] StartX=9 StartY=0 StartZ=0 EndX=9 EndY=-3 EndZ=0
    g23: LineSegment StartX=0 StartY=0 StartZ=0 EndX=9 EndY=0 EndZ=0
    g24: LineSegment StartX=9 StartY=0 StartZ=0 EndX=9 EndY=-3 EndZ=0
    g25: LineSegment StartX=9 StartY=-3 StartZ=0 EndX=6 EndY=-3 EndZ=0
    g26: LineSegment StartX=6 StartY=-3 StartZ=0 EndX=6 EndY=-8.6 EndZ=0
    g27: LineSegment StartX=6 StartY=-8.6 StartZ=0 EndX=9 EndY=-8.6 EndZ=0
    g28: LineSegment StartX=9 StartY=-8.6 StartZ=0 EndX=9 EndY=-11.6 EndZ=0
    g29: LineSegment StartX=9 StartY=-11.6 StartZ=0 EndX=0 EndY=-11.6 EndZ=0
    g30: LineSegment StartX=0 StartY=-11.6 StartZ=0 EndX=0 EndY=-8.6 EndZ=0
    g31: LineSegment StartX=0 StartY=-8.6 StartZ=0 EndX=3 EndY=-8.6 EndZ=0
    g32: LineSegment StartX=3 StartY=-8.6 StartZ=0 EndX=3 EndY=-3 EndZ=0
    g33: LineSegment StartX=3 StartY=-3 StartZ=0 EndX=0 EndY=-3 EndZ=0
    g34: LineSegment StartX=0 StartY=-3 StartZ=0 EndX=0 EndY=0 EndZ=0
    g35: GeomPoint X=4.5 Y=-5.8 Z=0
    g36: LineSegment StartX=-1 StartY=-12.6 StartZ=0 EndX=10 EndY=-12.6 EndZ=0
    g37: LineSegment StartX=10 StartY=-12.6 StartZ=0 EndX=10 EndY=1 EndZ=0
    g38: LineSegment StartX=10 StartY=1 StartZ=0 EndX=-1 EndY=1 EndZ=0
    g39: LineSegment StartX=-1 StartY=1 StartZ=0 EndX=-1 EndY=-12.6 EndZ=0
    g40: GeomPoint [constr] X=4.5 Y=-5.8 Z=0
  constraints (94):
    c: Coincident(g0,g1)
    c: Coincident(g1,g2)
    c: Coincident(g2,g3)
    c: Coincident(g3,g0)
    c: Vertical(g0)
    c: Vertical(g2)
    c: Horizontal(g1)
    c: Horizontal(g3)
    c: Symmetric(g0,g2,g4)
    c: Coincident(g5,g6)
    c: Coincident(g6,g7)
    c: Coincident(g7,g8)
    c: Coincident(g8,g5)
    c: Vertical(g5)
    c: Vertical(g7)
    c: Horizontal(g6)
    c: Horizontal(g8)
    c: Equal(g8,g1)
    c: Equal(g7,g2)
    c: Symmetric(g5,g7,g9)
    c: DistanceX(g3,g3) = 9
    c: DistanceY(g0,g0) = 3
    c: Coincident(g0,g-1)
    c: PointOnObject(g5,g-2)
    c: Coincident(g10,g4)
    c: Coincident(g10,g9)
    c: PointOnObject(g11,g10)
    c: PointOnObject(g12,g10)
    c: PointOnObject(g11,g1)
    c: PointOnObject(g12,g8)
    c: Coincident(g13,g14)
    c: Coincident(g14,g15)
    c: Coincident(g15,g16)
    c: Coincident(g16,g13)
    c: Vertical(g13)
    c: Vertical(g15)
    c: Horizontal(g14)
    c: Horizontal(g16)
    c: Coincident(g13,g11)
    c: Distance(g14,g14) = 1.5
    c: Coincident(g17,g18)
    c: Coincident(g18,g19)
    c: Coincident(g19,g20)
    c: Coincident(g20,g17)
    c: Horizontal(g17)
    c: Horizontal(g19)
    c: Vertical(g18)
    c: Vertical(g20)
    c: Coincident(g17,g11)
    c: Equal(g19,g14)
    c: PointOnObject(g12,g14)
    c: Coincident(g21,g0)
    c: Coincident(g21,g2)
    c: Coincident(g22,g2)
    c: Coincident(g22,g1)
    c: Coincident(g23,g0)
    c: Coincident(g23,g2)
    c: Coincident(g24,g2)
    c: Coincident(g24,g1)
    c: Coincident(g25,g1)
    c: Coincident(g25,g15)
    c: Coincident(g26,g15)
    c: Coincident(g26,g14)
    c: Coincident(g27,g14)
    c: Coincident(g27,g7)
    c: Coincident(g28,g7)
    c: Coincident(g28,g6)
    c: Coincident(g29,g6)
    c: Coincident(g29,g5)
    c: Coincident(g30,g5)
    c: Coincident(g30,g5)
    c: Coincident(g31,g5)
    c: Coincident(g31,g18)
    c: Coincident(g32,g18)
    c: Coincident(g32,g17)
    c: Coincident(g33,g17)
    c: Coincident(g33,g0)
    c: Coincident(g34,g0)
    c: Coincident(g34,g0)
    c: DistanceY(g15,g15) = 5.6
    c: Equal(g15,g18)
    c: Symmetric(g18,g15,g35)
    c: Coincident(g36,g37)
    c: Coincident(g37,g38)
    c: Coincident(g38,g39)
    c: Coincident(g39,g36)
    c: Horizontal(g36)
    c: Horizontal(g38)
    c: Vertical(g37)
    c: Vertical(g39)
    c: Symmetric(g38,g36,g40)
    c: Coincident(g40,g35)
    c: Distance(g38,g23) = 1
    c: Distance(g28,g37) = 1
FEATURE [Sketcher::SketchObject] Sketch009  label="SketchLeft001"
  ArcFitTolerance = 1e-06
  AttachmentSupport = -> [Pad010]
  ExternalTypes = [0,0]
  FullyConstrained = true
  MakeInternals = false
  MapMode = 5
  Placement = pos=(-1,0,0) rot=(0.57735,-0.57735,-0.57735;2.0944rad)
  sketch-geometry (22):
    g0: LineSegment StartX=1.3 StartY=-4.8 StartZ=0 EndX=1.3 EndY=-1.8 EndZ=0
    g1: LineSegment StartX=4.3 StartY=-4.8 StartZ=0 EndX=1.3 EndY=-4.8 EndZ=0
    g2: LineSegment StartX=4.3 StartY=-10.4 StartZ=0 EndX=4.3 EndY=-4.8 EndZ=0
    g3: LineSegment StartX=1.3 StartY=-10.4 StartZ=0 EndX=4.3 EndY=-10.4 EndZ=0
    g4: LineSegment StartX=1.3 StartY=-13.4 StartZ=0 EndX=1.3 EndY=-10.4 EndZ=0
    g5: LineSegment StartX=10.3 StartY=-13.4 StartZ=0 EndX=1.3 EndY=-13.4 EndZ=0
    g6: LineSegment StartX=10.3 StartY=-10.4 StartZ=0 EndX=10.3 EndY=-13.4 EndZ=0
    g7: LineSegment StartX=7.3 StartY=-10.4 StartZ=0 EndX=10.3 EndY=-10.4 EndZ=0
    g8: LineSegment StartX=7.3 StartY=-4.8 StartZ=0 EndX=7.3 EndY=-10.4 EndZ=0
    g9: LineSegment StartX=10.3 StartY=-4.8 StartZ=0 EndX=7.3 EndY=-4.8 EndZ=0
    g10: LineSegment StartX=10.3 StartY=-1.8 StartZ=0 EndX=10.3 EndY=-4.8 EndZ=0
    g11: LineSegment StartX=1.3 StartY=-1.8 StartZ=0 EndX=10.3 EndY=-1.8 EndZ=0
    g12: LineSegment StartX=11.3 StartY=-0.8 StartZ=0 EndX=11.3 EndY=-14.4 EndZ=0
    g13: LineSegment StartX=0.3 StartY=-0.8 StartZ=0 EndX=11.3 EndY=-0.8 EndZ=0
    g14: LineSegment StartX=0.3 StartY=-14.4 StartZ=0 EndX=0.3 EndY=-0.8 EndZ=0
    g15: LineSegment StartX=11.3 StartY=-14.4 StartZ=0 EndX=0.3 EndY=-14.4 EndZ=0
    g16: GeomPoint [constr] X=5.8 Y=-7.6 Z=0
    g17: GeomPoint [constr] X=5.8 Y=-7.6 Z=0
    g18: LineSegment [constr] StartX=5.8 StartY=-7.6 StartZ=0 EndX=5.8 EndY=-14.4 EndZ=0
    g19: LineSegment [constr] StartX=-1 StartY=-0.8 StartZ=0 EndX=-1 EndY=-14.4 EndZ=0
    g20: GeomPoint [constr] X=5.8 Y=-7.6 Z=0
    g21: LineSegment [constr] StartX=5.8 StartY=-7.6 StartZ=0 EndX=5.8 EndY=-14.4 EndZ=0
  constraints (56):
    c: Coincident(g13,g14)
    c: Coincident(g12,g13)
    c: Coincident(g12,g15)
    c: Coincident(g15,g14)
    c: Coincident(g6,g7)
    c: Coincident(g5,g6)
    c: Coincident(g7,g8)
    c: Coincident(g8,g9)
    c: Coincident(g9,g10)
    c: Coincident(g10,g11)
    c: Coincident(g0,g11)
    c: Coincident(g0,g1)
    c: Coincident(g1,g2)
    c: Coincident(g2,g3)
    c: Coincident(g3,g4)
    c: Coincident(g4,g5)
    c: Equal(g14,g12)
    c: Equal(g13,g15)
    c: Equal(g0,g4)
    c: Equal(g4,g6)
    c: Equal(g6,g10)
    c: Equal(g8,g2)
    c: Equal(g9,g1)
    c: Equal(g1,g3)
    c: Equal(g3,g7)
    c: Horizontal(g13)
    c: Horizontal(g11)
    c: Horizontal(g1)
    c: Horizontal(g9)
    c: Horizontal(g7)
    c: Horizontal(g3)
    c: Horizontal(g5)
    c: Vertical(g12)
    c: Vertical(g10)
    c: Vertical(g0)
    c: Vertical(g2)
    c: Vertical(g8)
    c: Vertical(g4)
    c: Symmetric(g12,g13,g16)
    c: Symmetric(g4,g10,g17)
    c: Coincident(g16,g17)
    c: Coincident(g18,g16)
    c: Symmetric(g15,g15,g18)
    c: Coincident(g19,g-4)
    c: PointOnObject(g19,g-6)
    c: Vertical(g19)
    c: Symmetric(g19,g-9,g20)
    c: Coincident(g21,g20)
    c: Symmetric(g-6,g-6,g21)
    c: Equal(g13,g-13)
    c: Equal(g10,g-16)
    c: Equal(g11,g-15)
    c: Equal(g8,g-18)
    c: Equal(g9,g-17)
    c: Equal(g12,g-12)
    c: Coincident(g18,g21)
FEATURE [PartDesign::Pad] Pad012  label="PadLeft001"
  BaseFeature = -> Pad010
  Direction = (-1,0,0)
  Length = 10
  Length2 = 10
  Profile = -> Sketch009
  ReferenceAxis = -> Sketch009 [N_Axis]
  Refine = true
  SideType = 0
  Suppressed = false
  Type = 0
  Type2 = 0
FEATURE [Sketcher::SketchObject] Sketch010  label="SketchRight001"
  ArcFitTolerance = 1e-06
  AttachmentSupport = -> [Pad012]
  ExternalGeometry = -> [Sketch009]
  ExternalTypes = [0,0,0,0,0,0,0,0,0,0,0,0,0,0,0,0]
  FullyConstrained = true
  MakeInternals = false
  MapMode = 5
  Placement = pos=(10,0,0) rot=(0.57735,0.57735,0.57735;2.0944rad)
FEATURE [PartDesign::Pad] Pad013  label="PadRight001"
  BaseFeature = -> Pad012
  Direction = (1,0,0)
  Length = 10
  Length2 = 10
  Profile = -> Sketch010
  ReferenceAxis = -> Sketch010 [N_Axis]
  Refine = true
  SideType = 0
  Suppressed = false
  Type = 0
  Type2 = 0
FEATURE [PartDesign::Fillet] Fillet010  label="FilletInside001"
  Base = -> Pad013 [Edge163,Edge166,Edge168,Edge170,Edge172,Edge174,Edge176,Edge178,Edge180,Edge184,Edge164,Edge102,Edge117,Edge119,Edge121,Edge123,Edge115,Edge113,Edge111,Edge109,Edge107,Edge105,Edge103,Edge127,Edge126,Edge147,Edge129,Edge131,Edge133,Edge135,Edge145,Edge143,Edge141,Edge139,Edge137,Edge89,Edge85,Edge83,Edge81,Edge91,+8 more]
  BaseFeature = -> Pad013
  Radius = 1
  Refine = true
  SupportTransform = false
  Suppressed = false
  UseAllEdges = false
FEATURE [PartDesign::Fillet] Fillet011  label="FilletBottom001"
  Base = -> Fillet010 [Face31]
  BaseFeature = -> Fillet010
  Radius = 0.5
  Refine = true
  SupportTransform = false
  Suppressed = false
  UseAllEdges = false
FEATURE [PartDesign::Fillet] Fillet012  label="FilletAroundJointEdge001"
  Base = -> Fillet011 [Face77,Face12,Face4,Face45]
  BaseFeature = -> Fillet011
  Radius = 0.3
  Refine = true
  SupportTransform = false
  Suppressed = false
  UseAllEdges = false
FEATURE [PartDesign::Fillet] Fillet015  label="FilletInsideAtBottom001"
  Base = -> Fillet009 [Face342,Face341,Face343,Face340,Face62]
  BaseFeature = -> Fillet009
  Radius = 1
  Refine = true
  SupportTransform = false
  Suppressed = false
  UseAllEdges = false
FEATURE [PartDesign::Body] Body001  label="Connector5WayCross"
  AllowCompound = true
  Group = -> [Binder001,Pad001,Pad002,Binder002,Pad003,Sketch001,Pad004,Sketch003,Pad006,Binder,Sketch004,Pad007,Fillet001,Fillet002,Fillet003,Fillet004,Fillet009,Fillet015]
  Origin = -> Origin002
  Tip = -> Fillet015
FEATURE [PartDesign::SubShapeBinder] Binder008
  BindCopyOnChange = 0
  BindMode = 0
  ClaimChildren = false
  Context = -> Body003 [Binder008.]
  Fuse = false
  MakeFace = true
  OffsetFill = false
  OffsetIntersection = false
  OffsetJoinType = 0
  OffsetOpenResult = false
  PartialLoad = false
  Refine = true
  Relative = true
  Support = -> [Sketch011]
  _Version = 2
FEATURE [App::Point] Origin015  label="Origin016"
  Role = Origin
FEATURE [App::Point] Origin017  label="Origin018"
  Role = Origin
FEATURE [PartDesign::Pad] Pad014
  Direction = (0,0,1)
  Length = 85
  Length2 = 10
  Profile = -> Binder008
  Refine = true
  SideType = 0
  Suppressed = false
  Type = 0
  Type2 = 0
FEATURE [PartDesign::Fillet] Fillet016
  Base = -> Pad014
  BaseFeature = -> Pad014
  Radius = 0.5
  Refine = true
  SupportTransform = false
  Suppressed = false
  UseAllEdges = true
FEATURE [PartDesign::Body] Body003  label="Rail85mm"
  AllowCompound = true
  Group = -> [Pad014,Fillet016,Binder008]
  Origin = -> Origin014
  Tip = -> Fillet016
FEATURE [Sketcher::SketchObject] Sketch011  label="MasterSketchPole001"
  ArcFitTolerance = 1e-06
  AttachmentSupport = -> [Origin016]
  ExternalTypes = [0]
  FullyConstrained = true
  MakeInternals = false
  MapMode = 5
  expr: Constraints[20] = 2.8 * 3
  expr: Constraints[39] = 2.8 / 2
  expr: Constraints[79] = 3 * 2
  sketch-geometry (37):
    g0: LineSegment [constr] StartX=0 StartY=0 StartZ=0 EndX=0 EndY=-2.8 EndZ=0
    g1: LineSegment [constr] StartX=0 StartY=-2.8 StartZ=0 EndX=8.4 EndY=-2.8 EndZ=0
    g2: LineSegment [constr] StartX=8.4 StartY=-2.8 StartZ=0 EndX=8.4 EndY=0 EndZ=0
    g3: LineSegment [constr] StartX=8.4 StartY=0 StartZ=0 EndX=0 EndY=0 EndZ=0
    g4: GeomPoint [constr] X=4.2 Y=-1.4 Z=0
    g5: LineSegment [constr] StartX=0 StartY=-8.8 StartZ=0 EndX=0 EndY=-11.6 EndZ=0
    g6: LineSegment [constr] StartX=0 StartY=-11.6 StartZ=0 EndX=8.4 EndY=-11.6 EndZ=0
    g7: LineSegment [constr] StartX=8.4 StartY=-11.6 StartZ=0 EndX=8.4 EndY=-8.8 EndZ=0
    g8: LineSegment [constr] StartX=8.4 StartY=-8.8 StartZ=0 EndX=0 EndY=-8.8 EndZ=0
    g9: GeomPoint [constr] X=4.2 Y=-10.2 Z=0
    g10: LineSegment [constr] StartX=4.2 StartY=-1.4 StartZ=0 EndX=4.2 EndY=-10.2 EndZ=0
    g11: GeomPoint [constr] X=4.2 Y=-2.8 Z=0
    g12: GeomPoint [constr] X=4.2 Y=-8.8 Z=0
    g13: LineSegment [constr] StartX=4.2 StartY=-2.8 StartZ=0 EndX=4.2 EndY=-8.8 EndZ=0
    g14: LineSegment [constr] StartX=4.2 StartY=-8.8 StartZ=0 EndX=5.6 EndY=-8.8 EndZ=0
    g15: LineSegment [constr] StartX=5.6 StartY=-8.8 StartZ=0 EndX=5.6 EndY=-2.8 EndZ=0
    g16: LineSegment [constr] StartX=5.6 StartY=-2.8 StartZ=0 EndX=4.2 EndY=-2.8 EndZ=0
    g17: LineSegment [constr] StartX=4.2 StartY=-2.8 StartZ=0 EndX=2.8 EndY=-2.8 EndZ=0
    g18: LineSegment [constr] StartX=2.8 StartY=-2.8 StartZ=0 EndX=2.8 EndY=-8.8 EndZ=0
    g19: LineSegment [constr] StartX=2.8 StartY=-8.8 StartZ=0 EndX=4.2 EndY=-8.8 EndZ=0
    g20: LineSegment [constr] StartX=4.2 StartY=-8.8 StartZ=0 EndX=4.2 EndY=-2.8 EndZ=0
    g21: LineSegment [constr] StartX=0 StartY=0 StartZ=0 EndX=8.4 EndY=0 EndZ=0
    g22: LineSegment [constr] StartX=8.4 StartY=0 StartZ=0 EndX=8.4 EndY=-2.8 EndZ=0
    g23: LineSegment StartX=0 StartY=0 StartZ=0 EndX=8.4 EndY=0 EndZ=0
    g24: LineSegment StartX=8.4 StartY=0 StartZ=0 EndX=8.4 EndY=-2.8 EndZ=0
    g25: LineSegment StartX=8.4 StartY=-2.8 StartZ=0 EndX=5.6 EndY=-2.8 EndZ=0
    g26: LineSegment StartX=5.6 StartY=-2.8 StartZ=0 EndX=5.6 EndY=-8.8 EndZ=0
    g27: LineSegment StartX=5.6 StartY=-8.8 StartZ=0 EndX=8.4 EndY=-8.8 EndZ=0
    g28: LineSegment StartX=8.4 StartY=-8.8 StartZ=0 EndX=8.4 EndY=-11.6 EndZ=0
    g29: LineSegment StartX=8.4 StartY=-11.6 StartZ=0 EndX=0 EndY=-11.6 EndZ=0
    g30: LineSegment StartX=0 StartY=-11.6 StartZ=0 EndX=0 EndY=-8.8 EndZ=0
    g31: LineSegment StartX=0 StartY=-8.8 StartZ=0 EndX=2.8 EndY=-8.8 EndZ=0
    g32: LineSegment StartX=2.8 StartY=-8.8 StartZ=0 EndX=2.8 EndY=-2.8 EndZ=0
    g33: LineSegment StartX=2.8 StartY=-2.8 StartZ=0 EndX=0 EndY=-2.8 EndZ=0
    g34: LineSegment StartX=0 StartY=-2.8 StartZ=0 EndX=0 EndY=0 EndZ=0
    g35: GeomPoint X=4.2 Y=-5.8 Z=0
    g36: GeomPoint [constr] X=4.2 Y=-5.8 Z=0
  constraints (83):
    c: Coincident(g0,g1)
    c: Coincident(g1,g2)
    c: Coincident(g2,g3)
    c: Coincident(g3,g0)
    c: Vertical(g0)
    c: Vertical(g2)
    c: Horizontal(g1)
    c: Horizontal(g3)
    c: Symmetric(g0,g2,g4)
    c: Coincident(g5,g6)
    c: Coincident(g6,g7)
    c: Coincident(g7,g8)
    c: Coincident(g8,g5)
    c: Vertical(g5)
    c: Vertical(g7)
    c: Horizontal(g6)
    c: Horizontal(g8)
    c: Equal(g8,g1)
    c: Equal(g7,g2)
    c: Symmetric(g5,g7,g9)
    c: DistanceX(g3,g3) = 8.4
    c: DistanceY(g0,g0) = 2.8
    c: Coincident(g0,g-1)
    c: PointOnObject(g5,g-2)
    c: Coincident(g10,g4)
    c: Coincident(g10,g9)
    c: PointOnObject(g11,g10)
    c: PointOnObject(g12,g10)
    c: PointOnObject(g11,g1)
    c: PointOnObject(g12,g8)
    c: Coincident(g13,g14)
    c: Coincident(g14,g15)
    c: Coincident(g15,g16)
    c: Coincident(g16,g13)
    c: Vertical(g13)
    c: Vertical(g15)
    c: Horizontal(g14)
    c: Horizontal(g16)
    c: Coincident(g13,g11)
    c: Distance(g14,g14) = 1.4
    c: Coincident(g17,g18)
    c: Coincident(g18,g19)
    c: Coincident(g19,g20)
    c: Coincident(g20,g17)
    c: Horizontal(g17)
    c: Horizontal(g19)
    c: Vertical(g18)
    c: Vertical(g20)
    c: Coincident(g17,g11)
    c: Equal(g19,g14)
    c: PointOnObject(g12,g14)
    c: Coincident(g21,g0)
    c: Coincident(g21,g2)
    c: Coincident(g22,g2)
    c: Coincident(g22,g1)
    c: Coincident(g23,g0)
    c: Coincident(g23,g2)
    c: Coincident(g24,g2)
    c: Coincident(g24,g1)
    c: Coincident(g25,g1)
    c: Coincident(g25,g15)
    c: Coincident(g26,g15)
    c: Coincident(g26,g14)
    c: Coincident(g27,g14)
    c: Coincident(g27,g7)
    c: Coincident(g28,g7)
    c: Coincident(g28,g6)
    c: Coincident(g29,g6)
    c: Coincident(g29,g5)
    c: Coincident(g30,g5)
    c: Coincident(g30,g5)
    c: Coincident(g31,g5)
    c: Coincident(g31,g18)
    c: Coincident(g32,g18)
    c: Coincident(g32,g17)
    c: Coincident(g33,g17)
    c: Coincident(g33,g0)
    c: Coincident(g34,g0)
    c: Coincident(g34,g0)
    c: DistanceY(g15,g15) = 6
    c: Equal(g15,g18)
    c: Symmetric(g18,g15,g35)
    c: Coincident(g36,g35)
FEATURE [PartDesign::SubShapeBinder] Binder009
  BindCopyOnChange = 0
  BindMode = 0
  ClaimChildren = false
  Context = -> Body004 [Binder009.]
  Fuse = false
  MakeFace = true
  OffsetFill = false
  OffsetIntersection = false
  OffsetJoinType = 0
  OffsetOpenResult = false
  PartialLoad = false
  Refine = true
  Relative = true
  Support = -> [Sketch012]
  _Version = 2
FEATURE [App::Point] Origin019  label="Origin020"
  Role = Origin
FEATURE [App::Point] Origin021  label="Origin022"
  Role = Origin
FEATURE [Sketcher::SketchObject] Sketch012  label="MasterSketchPole002"
  ArcFitTolerance = 1e-06
  AttachmentSupport = -> [Origin020]
  ExternalTypes = [0]
  FullyConstrained = true
  MakeInternals = false
  MapMode = 5
  expr: Constraints[20] = 2.8 * 3
  expr: Constraints[39] = 2.8 / 2
  expr: Constraints[79] = 3 * 2
  sketch-geometry (37):
    g0: LineSegment [constr] StartX=0 StartY=0 StartZ=0 EndX=0 EndY=-2.8 EndZ=0
    g1: LineSegment [constr] StartX=0 StartY=-2.8 StartZ=0 EndX=8.4 EndY=-2.8 EndZ=0
    g2: LineSegment [constr] StartX=8.4 StartY=-2.8 StartZ=0 EndX=8.4 EndY=0 EndZ=0
    g3: LineSegment [constr] StartX=8.4 StartY=0 StartZ=0 EndX=0 EndY=0 EndZ=0
    g4: GeomPoint [constr] X=4.2 Y=-1.4 Z=0
    g5: LineSegment [constr] StartX=0 StartY=-8.8 StartZ=0 EndX=0 EndY=-11.6 EndZ=0
    g6: LineSegment [constr] StartX=0 StartY=-11.6 StartZ=0 EndX=8.4 EndY=-11.6 EndZ=0
    g7: LineSegment [constr] StartX=8.4 StartY=-11.6 StartZ=0 EndX=8.4 EndY=-8.8 EndZ=0
    g8: LineSegment [constr] StartX=8.4 StartY=-8.8 StartZ=0 EndX=0 EndY=-8.8 EndZ=0
    g9: GeomPoint [constr] X=4.2 Y=-10.2 Z=0
    g10: LineSegment [constr] StartX=4.2 StartY=-1.4 StartZ=0 EndX=4.2 EndY=-10.2 EndZ=0
    g11: GeomPoint [constr] X=4.2 Y=-2.8 Z=0
    g12: GeomPoint [constr] X=4.2 Y=-8.8 Z=0
    g13: LineSegment [constr] StartX=4.2 StartY=-2.8 StartZ=0 EndX=4.2 EndY=-8.8 EndZ=0
    g14: LineSegment [constr] StartX=4.2 StartY=-8.8 StartZ=0 EndX=5.6 EndY=-8.8 EndZ=0
    g15: LineSegment [constr] StartX=5.6 StartY=-8.8 StartZ=0 EndX=5.6 EndY=-2.8 EndZ=0
    g16: LineSegment [constr] StartX=5.6 StartY=-2.8 StartZ=0 EndX=4.2 EndY=-2.8 EndZ=0
    g17: LineSegment [constr] StartX=4.2 StartY=-2.8 StartZ=0 EndX=2.8 EndY=-2.8 EndZ=0
    g18: LineSegment [constr] StartX=2.8 StartY=-2.8 StartZ=0 EndX=2.8 EndY=-8.8 EndZ=0
    g19: LineSegment [constr] StartX=2.8 StartY=-8.8 StartZ=0 EndX=4.2 EndY=-8.8 EndZ=0
    g20: LineSegment [constr] StartX=4.2 StartY=-8.8 StartZ=0 EndX=4.2 EndY=-2.8 EndZ=0
    g21: LineSegment [constr] StartX=0 StartY=0 StartZ=0 EndX=8.4 EndY=0 EndZ=0
    g22: LineSegment [constr] StartX=8.4 StartY=0 StartZ=0 EndX=8.4 EndY=-2.8 EndZ=0
    g23: LineSegment StartX=0 StartY=0 StartZ=0 EndX=8.4 EndY=0 EndZ=0
    g24: LineSegment StartX=8.4 StartY=0 StartZ=0 EndX=8.4 EndY=-2.8 EndZ=0
    g25: LineSegment StartX=8.4 StartY=-2.8 StartZ=0 EndX=5.6 EndY=-2.8 EndZ=0
    g26: LineSegment StartX=5.6 StartY=-2.8 StartZ=0 EndX=5.6 EndY=-8.8 EndZ=0
    g27: LineSegment StartX=5.6 StartY=-8.8 StartZ=0 EndX=8.4 EndY=-8.8 EndZ=0
    g28: LineSegment StartX=8.4 StartY=-8.8 StartZ=0 EndX=8.4 EndY=-11.6 EndZ=0
    g29: LineSegment StartX=8.4 StartY=-11.6 StartZ=0 EndX=0 EndY=-11.6 EndZ=0
    g30: LineSegment StartX=0 StartY=-11.6 StartZ=0 EndX=0 EndY=-8.8 EndZ=0
    g31: LineSegment StartX=0 StartY=-8.8 StartZ=0 EndX=2.8 EndY=-8.8 EndZ=0
    g32: LineSegment StartX=2.8 StartY=-8.8 StartZ=0 EndX=2.8 EndY=-2.8 EndZ=0
    g33: LineSegment StartX=2.8 StartY=-2.8 StartZ=0 EndX=0 EndY=-2.8 EndZ=0
    g34: LineSegment StartX=0 StartY=-2.8 StartZ=0 EndX=0 EndY=0 EndZ=0
    g35: GeomPoint X=4.2 Y=-5.8 Z=0
    g36: GeomPoint [constr] X=4.2 Y=-5.8 Z=0
  constraints (83):
    c: Coincident(g0,g1)
    c: Coincident(g1,g2)
    c: Coincident(g2,g3)
    c: Coincident(g3,g0)
    c: Vertical(g0)
    c: Vertical(g2)
    c: Horizontal(g1)
    c: Horizontal(g3)
    c: Symmetric(g0,g2,g4)
    c: Coincident(g5,g6)
    c: Coincident(g6,g7)
    c: Coincident(g7,g8)
    c: Coincident(g8,g5)
    c: Vertical(g5)
    c: Vertical(g7)
    c: Horizontal(g6)
    c: Horizontal(g8)
    c: Equal(g8,g1)
    c: Equal(g7,g2)
    c: Symmetric(g5,g7,g9)
    c: DistanceX(g3,g3) = 8.4
    c: DistanceY(g0,g0) = 2.8
    c: Coincident(g0,g-1)
    c: PointOnObject(g5,g-2)
    c: Coincident(g10,g4)
    c: Coincident(g10,g9)
    c: PointOnObject(g11,g10)
    c: PointOnObject(g12,g10)
    c: PointOnObject(g11,g1)
    c: PointOnObject(g12,g8)
    c: Coincident(g13,g14)
    c: Coincident(g14,g15)
    c: Coincident(g15,g16)
    c: Coincident(g16,g13)
    c: Vertical(g13)
    c: Vertical(g15)
    c: Horizontal(g14)
    c: Horizontal(g16)
    c: Coincident(g13,g11)
    c: Distance(g14,g14) = 1.4
    c: Coincident(g17,g18)
    c: Coincident(g18,g19)
    c: Coincident(g19,g20)
    c: Coincident(g20,g17)
    c: Horizontal(g17)
    c: Horizontal(g19)
    c: Vertical(g18)
    c: Vertical(g20)
    c: Coincident(g17,g11)
    c: Equal(g19,g14)
    c: PointOnObject(g12,g14)
    c: Coincident(g21,g0)
    c: Coincident(g21,g2)
    c: Coincident(g22,g2)
    c: Coincident(g22,g1)
    c: Coincident(g23,g0)
    c: Coincident(g23,g2)
    c: Coincident(g24,g2)
    c: Coincident(g24,g1)
    c: Coincident(g25,g1)
    c: Coincident(g25,g15)
    c: Coincident(g26,g15)
    c: Coincident(g26,g14)
    c: Coincident(g27,g14)
    c: Coincident(g27,g7)
    c: Coincident(g28,g7)
    c: Coincident(g28,g6)
    c: Coincident(g29,g6)
    c: Coincident(g29,g5)
    c: Coincident(g30,g5)
    c: Coincident(g30,g5)
    c: Coincident(g31,g5)
    c: Coincident(g31,g18)
    c: Coincident(g32,g18)
    c: Coincident(g32,g17)
    c: Coincident(g33,g17)
    c: Coincident(g33,g0)
    c: Coincident(g34,g0)
    c: Coincident(g34,g0)
    c: DistanceY(g15,g15) = 6
    c: Equal(g15,g18)
    c: Symmetric(g18,g15,g35)
    c: Coincident(g36,g35)
FEATURE [PartDesign::SubShapeBinder] Binder010
  BindCopyOnChange = 0
  BindMode = 0
  ClaimChildren = false
  Context = -> Body005 [Binder010.]
  Fuse = false
  MakeFace = true
  OffsetFill = false
  OffsetIntersection = false
  OffsetJoinType = 0
  OffsetOpenResult = false
  PartialLoad = false
  Refine = true
  Relative = true
  Support = -> [Sketch013]
  _Version = 2
FEATURE [App::Point] Origin023  label="Origin024"
  Role = Origin
FEATURE [App::Point] Origin025  label="Origin026"
  Role = Origin
FEATURE [PartDesign::Pad] Pad016
  Direction = (0,0,1)
  Length = 65
  Length2 = 10
  Profile = -> Binder010
  Refine = true
  SideType = 0
  Suppressed = false
  Type = 0
  Type2 = 0
FEATURE [PartDesign::Fillet] Fillet018
  Base = -> Pad016
  BaseFeature = -> Pad016
  Radius = 0.5
  Refine = true
  SupportTransform = false
  Suppressed = false
  UseAllEdges = true
FEATURE [PartDesign::Body] Body005  label="Rail65mm"
  AllowCompound = true
  Group = -> [Pad016,Fillet018,Binder010]
  Origin = -> Origin022
  Tip = -> Fillet018
FEATURE [Sketcher::SketchObject] Sketch013  label="MasterSketchPole003"
  ArcFitTolerance = 1e-06
  AttachmentSupport = -> [Origin024]
  ExternalTypes = [0]
  FullyConstrained = true
  MakeInternals = false
  MapMode = 5
  expr: Constraints[20] = 2.8 * 3
  expr: Constraints[39] = 2.8 / 2
  expr: Constraints[79] = 3 * 2
  sketch-geometry (37):
    g0: LineSegment [constr] StartX=0 StartY=0 StartZ=0 EndX=0 EndY=-2.8 EndZ=0
    g1: LineSegment [constr] StartX=0 StartY=-2.8 StartZ=0 EndX=8.4 EndY=-2.8 EndZ=0
    g2: LineSegment [constr] StartX=8.4 StartY=-2.8 StartZ=0 EndX=8.4 EndY=0 EndZ=0
    g3: LineSegment [constr] StartX=8.4 StartY=0 StartZ=0 EndX=0 EndY=0 EndZ=0
    g4: GeomPoint [constr] X=4.2 Y=-1.4 Z=0
    g5: LineSegment [constr] StartX=0 StartY=-8.8 StartZ=0 EndX=0 EndY=-11.6 EndZ=0
    g6: LineSegment [constr] StartX=0 StartY=-11.6 StartZ=0 EndX=8.4 EndY=-11.6 EndZ=0
    g7: LineSegment [constr] StartX=8.4 StartY=-11.6 StartZ=0 EndX=8.4 EndY=-8.8 EndZ=0
    g8: LineSegment [constr] StartX=8.4 StartY=-8.8 StartZ=0 EndX=0 EndY=-8.8 EndZ=0
    g9: GeomPoint [constr] X=4.2 Y=-10.2 Z=0
    g10: LineSegment [constr] StartX=4.2 StartY=-1.4 StartZ=0 EndX=4.2 EndY=-10.2 EndZ=0
    g11: GeomPoint [constr] X=4.2 Y=-2.8 Z=0
    g12: GeomPoint [constr] X=4.2 Y=-8.8 Z=0
    g13: LineSegment [constr] StartX=4.2 StartY=-2.8 StartZ=0 EndX=4.2 EndY=-8.8 EndZ=0
    g14: LineSegment [constr] StartX=4.2 StartY=-8.8 StartZ=0 EndX=5.6 EndY=-8.8 EndZ=0
    g15: LineSegment [constr] StartX=5.6 StartY=-8.8 StartZ=0 EndX=5.6 EndY=-2.8 EndZ=0
    g16: LineSegment [constr] StartX=5.6 StartY=-2.8 StartZ=0 EndX=4.2 EndY=-2.8 EndZ=0
    g17: LineSegment [constr] StartX=4.2 StartY=-2.8 StartZ=0 EndX=2.8 EndY=-2.8 EndZ=0
    g18: LineSegment [constr] StartX=2.8 StartY=-2.8 StartZ=0 EndX=2.8 EndY=-8.8 EndZ=0
    g19: LineSegment [constr] StartX=2.8 StartY=-8.8 StartZ=0 EndX=4.2 EndY=-8.8 EndZ=0
    g20: LineSegment [constr] StartX=4.2 StartY=-8.8 StartZ=0 EndX=4.2 EndY=-2.8 EndZ=0
    g21: LineSegment [constr] StartX=0 StartY=0 StartZ=0 EndX=8.4 EndY=0 EndZ=0
    g22: LineSegment [constr] StartX=8.4 StartY=0 StartZ=0 EndX=8.4 EndY=-2.8 EndZ=0
    g23: LineSegment StartX=0 StartY=0 StartZ=0 EndX=8.4 EndY=0 EndZ=0
    g24: LineSegment StartX=8.4 StartY=0 StartZ=0 EndX=8.4 EndY=-2.8 EndZ=0
    g25: LineSegment StartX=8.4 StartY=-2.8 StartZ=0 EndX=5.6 EndY=-2.8 EndZ=0
    g26: LineSegment StartX=5.6 StartY=-2.8 StartZ=0 EndX=5.6 EndY=-8.8 EndZ=0
    g27: LineSegment StartX=5.6 StartY=-8.8 StartZ=0 EndX=8.4 EndY=-8.8 EndZ=0
    g28: LineSegment StartX=8.4 StartY=-8.8 StartZ=0 EndX=8.4 EndY=-11.6 EndZ=0
    g29: LineSegment StartX=8.4 StartY=-11.6 StartZ=0 EndX=0 EndY=-11.6 EndZ=0
    g30: LineSegment StartX=0 StartY=-11.6 StartZ=0 EndX=0 EndY=-8.8 EndZ=0
    g31: LineSegment StartX=0 StartY=-8.8 StartZ=0 EndX=2.8 EndY=-8.8 EndZ=0
    g32: LineSegment StartX=2.8 StartY=-8.8 StartZ=0 EndX=2.8 EndY=-2.8 EndZ=0
    g33: LineSegment StartX=2.8 StartY=-2.8 StartZ=0 EndX=0 EndY=-2.8 EndZ=0
    g34: LineSegment StartX=0 StartY=-2.8 StartZ=0 EndX=0 EndY=0 EndZ=0
    g35: GeomPoint X=4.2 Y=-5.8 Z=0
    g36: GeomPoint [constr] X=4.2 Y=-5.8 Z=0
  constraints (83):
    c: Coincident(g0,g1)
    c: Coincident(g1,g2)
    c: Coincident(g2,g3)
    c: Coincident(g3,g0)
    c: Vertical(g0)
    c: Vertical(g2)
    c: Horizontal(g1)
    c: Horizontal(g3)
    c: Symmetric(g0,g2,g4)
    c: Coincident(g5,g6)
    c: Coincident(g6,g7)
    c: Coincident(g7,g8)
    c: Coincident(g8,g5)
    c: Vertical(g5)
    c: Vertical(g7)
    c: Horizontal(g6)
    c: Horizontal(g8)
    c: Equal(g8,g1)
    c: Equal(g7,g2)
    c: Symmetric(g5,g7,g9)
    c: DistanceX(g3,g3) = 8.4
    c: DistanceY(g0,g0) = 2.8
    c: Coincident(g0,g-1)
    c: PointOnObject(g5,g-2)
    c: Coincident(g10,g4)
    c: Coincident(g10,g9)
    c: PointOnObject(g11,g10)
    c: PointOnObject(g12,g10)
    c: PointOnObject(g11,g1)
    c: PointOnObject(g12,g8)
    c: Coincident(g13,g14)
    c: Coincident(g14,g15)
    c: Coincident(g15,g16)
    c: Coincident(g16,g13)
    c: Vertical(g13)
    c: Vertical(g15)
    c: Horizontal(g14)
    c: Horizontal(g16)
    c: Coincident(g13,g11)
    c: Distance(g14,g14) = 1.4
    c: Coincident(g17,g18)
    c: Coincident(g18,g19)
    c: Coincident(g19,g20)
    c: Coincident(g20,g17)
    c: Horizontal(g17)
    c: Horizontal(g19)
    c: Vertical(g18)
    c: Vertical(g20)
    c: Coincident(g17,g11)
    c: Equal(g19,g14)
    c: PointOnObject(g12,g14)
    c: Coincident(g21,g0)
    c: Coincident(g21,g2)
    c: Coincident(g22,g2)
    c: Coincident(g22,g1)
    c: Coincident(g23,g0)
    c: Coincident(g23,g2)
    c: Coincident(g24,g2)
    c: Coincident(g24,g1)
    c: Coincident(g25,g1)
    c: Coincident(g25,g15)
    c: Coincident(g26,g15)
    c: Coincident(g26,g14)
    c: Coincident(g27,g14)
    c: Coincident(g27,g7)
    c: Coincident(g28,g7)
    c: Coincident(g28,g6)
    c: Coincident(g29,g6)
    c: Coincident(g29,g5)
    c: Coincident(g30,g5)
    c: Coincident(g30,g5)
    c: Coincident(g31,g5)
    c: Coincident(g31,g18)
    c: Coincident(g32,g18)
    c: Coincident(g32,g17)
    c: Coincident(g33,g17)
    c: Coincident(g33,g0)
    c: Coincident(g34,g0)
    c: Coincident(g34,g0)
    c: DistanceY(g15,g15) = 6
    c: Equal(g15,g18)
    c: Symmetric(g18,g15,g35)
    c: Coincident(g36,g35)
FEATURE [App::Point] Origin027  label="Origin028"
  Role = Origin
FEATURE [PartDesign::SubShapeBinder] Binder011
  BindCopyOnChange = 0
  BindMode = 0
  ClaimChildren = false
  Context = -> Body006 [Binder011.]
  Fuse = false
  MakeFace = true
  OffsetFill = false
  OffsetIntersection = false
  OffsetJoinType = 0
  OffsetOpenResult = false
  PartialLoad = false
  Refine = true
  Relative = true
  Support = -> [Sketch]
  _Version = 2
FEATURE [Sketcher::SketchObject] Sketch014
  ArcFitTolerance = 1e-06
  AttachmentSupport = -> [Origin026]
  ExternalGeometry = -> [Binder011]
  ExternalTypes = [0]
  FullyConstrained = true
  MakeInternals = false
  MapMode = 5
FEATURE [PartDesign::Pad] Pad017
  Direction = (0,0,1)
  Length = 10
  Length2 = 10
  Profile = -> Sketch014
  ReferenceAxis = -> Sketch014 [N_Axis]
  Refine = true
  SideType = 0
  Suppressed = false
  Type = 0
  Type2 = 0
FEATURE [Sketcher::SketchObject] Sketch015
  ArcFitTolerance = 1e-06
  AttachmentSupport = -> [Origin026]
  ExternalGeometry = -> [Pad017]
  ExternalTypes = [0,0,0,0]
  FullyConstrained = true
  MakeInternals = false
  MapMode = 5
FEATURE [PartDesign::Pad] Pad018
  BaseFeature = -> Pad017
  Direction = (0,0,1)
  Length = 13.6
  Length2 = 10
  Profile = -> Sketch015
  ReferenceAxis = -> Sketch015 [N_Axis]
  Refine = true
  Reversed = true
  SideType = 0
  Suppressed = false
  Type = 0
  Type2 = 0
  expr: Length = 2 + 3 + 3 + 5.6
FEATURE [Sketcher::SketchObject] Sketch016
  ArcFitTolerance = 1e-06
  AttachmentOffset = pos=(0,0,-1) rot=(0,0,1;0rad)
  AttachmentSupport = -> [Origin026]
  ExternalGeometry = -> [Pad018]
  ExternalTypes = [0]
  FullyConstrained = true
  MakeInternals = false
  MapMode = 5
  Placement = pos=(0,1,-2e-16) rot=(1,0,0;1.5708rad)
  sketch-geometry (32):
    g0: LineSegment [constr] StartX=10 StartY=-3.6e-15 StartZ=0 EndX=-1 EndY=-3.6e-15 EndZ=0
    g1: LineSegment [constr] StartX=-5.3071e-12 StartY=-1 StartZ=0 EndX=-5.3071e-12 EndY=-4 EndZ=0
    g2: LineSegment [constr] StartX=-5.3071e-12 StartY=-4 StartZ=0 EndX=9 EndY=-4 EndZ=0
    g3: LineSegment [constr] StartX=9 StartY=-4 StartZ=0 EndX=9 EndY=-1 EndZ=0
    g4: LineSegment [constr] StartX=9 StartY=-1 StartZ=0 EndX=-5.3078e-12 EndY=-1 EndZ=0
    g5: LineSegment [constr] StartX=-5.3078e-12 StartY=-9.6 StartZ=0 EndX=-5.3078e-12 EndY=-12.6 EndZ=0
    g6: LineSegment [constr] StartX=-5.3078e-12 StartY=-12.6 StartZ=0 EndX=9 EndY=-12.6 EndZ=0
    g7: LineSegment [constr] StartX=9 StartY=-12.6 StartZ=0 EndX=9 EndY=-9.6 EndZ=0
    g8: LineSegment [constr] StartX=9 StartY=-9.6 StartZ=0 EndX=-5.3078e-12 EndY=-9.6 EndZ=0
    g9: LineSegment [constr] StartX=3 StartY=-4 StartZ=0 EndX=3 EndY=-9.6 EndZ=0
    g10: LineSegment [constr] StartX=3 StartY=-9.6 StartZ=0 EndX=6 EndY=-9.6 EndZ=0
    g11: LineSegment [constr] StartX=6 StartY=-9.6 StartZ=0 EndX=6 EndY=-4 EndZ=0
    g12: LineSegment [constr] StartX=6 StartY=-4 StartZ=0 EndX=3 EndY=-4 EndZ=0
    g13: GeomPoint [constr] X=4.5 Y=-4 Z=0
    g14: GeomPoint [constr] X=4.5 Y=-6.8 Z=0
    g15: GeomPoint [constr] X=4.5 Y=-9.6 Z=0
    g16: LineSegment StartX=-1 StartY=-3.6e-15 StartZ=0 EndX=-1 EndY=-13.6 EndZ=0
    g17: LineSegment StartX=-1 StartY=-13.6 StartZ=0 EndX=10 EndY=-13.6 EndZ=0
    g18: LineSegment StartX=10 StartY=-13.6 StartZ=0 EndX=10 EndY=-3.6e-15 EndZ=0
    g19: LineSegment StartX=10 StartY=-3.6e-15 StartZ=0 EndX=-1 EndY=-3.6e-15 EndZ=0
    g20: LineSegment StartX=-5.3071e-12 StartY=-1 StartZ=0 EndX=9 EndY=-1 EndZ=0
    g21: LineSegment StartX=9 StartY=-1 StartZ=0 EndX=9 EndY=-4 EndZ=0
    g22: LineSegment StartX=9 StartY=-4 StartZ=0 EndX=6 EndY=-4 EndZ=0
    g23: LineSegment StartX=6 StartY=-4 StartZ=0 EndX=6 EndY=-9.6 EndZ=0
    g24: LineSegment StartX=6 StartY=-9.6 StartZ=0 EndX=9 EndY=-9.6 EndZ=0
    g25: LineSegment StartX=9 StartY=-9.6 StartZ=0 EndX=9 EndY=-12.6 EndZ=0
    g26: LineSegment StartX=9 StartY=-12.6 StartZ=0 EndX=-5.3078e-12 EndY=-12.6 EndZ=0
    g27: LineSegment StartX=-5.3078e-12 StartY=-12.6 StartZ=0 EndX=-5.3078e-12 EndY=-9.6 EndZ=0
    g28: LineSegment StartX=-5.3078e-12 StartY=-9.6 StartZ=0 EndX=3 EndY=-9.6 EndZ=0
    g29: LineSegment StartX=3 StartY=-9.6 StartZ=0 EndX=3 EndY=-4 EndZ=0
    g30: LineSegment StartX=3 StartY=-4 StartZ=0 EndX=-5.3073e-12 EndY=-4 EndZ=0
    g31: LineSegment StartX=-5.3071e-12 StartY=-4 StartZ=0 EndX=-5.3071e-12 EndY=-1 EndZ=0
  constraints (74):
    c: Horizontal(g0)
    c: PointOnObject(g0,g-3)
    c: PointOnObject(g0,g-5)
    c: Distance(g-6,g0) = 10
    c: Coincident(g1,g2)
    c: Coincident(g2,g3)
    c: Coincident(g3,g4)
    c: Coincident(g4,g1)
    c: Vertical(g1)
    c: Vertical(g3)
    c: Horizontal(g2)
    c: Horizontal(g4)
    c: Distance(g1,g3) = 9
    c: Distance(g2,g4) = 3
    c: Coincident(g5,g6)
    c: Coincident(g6,g7)
    c: Coincident(g7,g8)
    c: Coincident(g8,g5)
    c: Vertical(g5)
    c: Vertical(g7)
    c: Horizontal(g6)
    c: Horizontal(g8)
    c: Distance(g5,g7) = 9
    c: Distance(g6,g8) = 3
    c: Coincident(g9,g10)
    c: Coincident(g10,g11)
    c: Coincident(g11,g12)
    c: Coincident(g12,g9)
    c: Vertical(g9)
    c: Vertical(g11)
    c: Horizontal(g10)
    c: Horizontal(g12)
    c: Distance(g9,g11) = 3
    c: Distance(g10,g12) = 5.6
    c: Symmetric(g5,g7,g15)
    c: Symmetric(g9,g10,g15)
    c: Symmetric(g1,g2,g13)
    c: Symmetric(g9,g11,g13)
    c: Symmetric(g9,g11,g14)
    c: Symmetric(g-4,g0,g14)
    c: Coincident(g16,g17)
    c: Coincident(g17,g18)
    c: Coincident(g18,g19)
    c: Coincident(g19,g16)
    c: Vertical(g16)
    c: Vertical(g18)
    c: Horizontal(g17)
    c: Horizontal(g19)
    c: Coincident(g16,g0)
    c: Coincident(g17,g-5)
    c: Coincident(g20,g1)
    c: Coincident(g20,g3)
    c: Coincident(g21,g3)
    c: Coincident(g21,g2)
    c: Coincident(g22,g2)
    c: Coincident(g22,g11)
    c: Coincident(g23,g11)
    c: Coincident(g23,g10)
    c: Coincident(g24,g10)
    c: Coincident(g24,g7)
    c: Coincident(g25,g7)
    c: Coincident(g25,g6)
    c: Coincident(g26,g6)
    c: Coincident(g26,g5)
    c: Coincident(g27,g5)
    c: Coincident(g27,g5)
    c: Coincident(g28,g5)
    c: Coincident(g28,g9)
    c: Coincident(g29,g9)
    c: Coincident(g29,g9)
    c: Coincident(g30,g9)
    c: Coincident(g30,g1)
    c: Coincident(g31,g1)
    c: Coincident(g31,g1)
FEATURE [PartDesign::Pad] Pad019
  BaseFeature = -> Pad018
  Direction = (0,-1,2e-16)
  Length = 10
  Length2 = 10
  Profile = -> Sketch016
  ReferenceAxis = -> Sketch016 [N_Axis]
  Refine = true
  Reversed = true
  SideType = 0
  Suppressed = false
  Type = 0
  Type2 = 0
FEATURE [PartDesign::Pad] Pad020
  BaseFeature = -> Pad019
  Direction = (0,-1,2e-16)
  Length = 23.6
  Length2 = 10
  Profile = -> Sketch016
  ReferenceAxis = -> Sketch016 [N_Axis]
  Refine = true
  SideType = 0
  Suppressed = false
  Type = 0
  Type2 = 0
  expr: Length = 10 + 2 + 3 + 3 + 5.6
FEATURE [Sketcher::SketchObject] Sketch017
  ArcFitTolerance = 1e-06
  AttachmentSupport = -> [Pad020]
  ExternalGeometry = -> [Pad020]
  ExternalTypes = [0]
  FullyConstrained = true
  MakeInternals = false
  MapMode = 5
  Placement = pos=(10,0,0) rot=(0.57735,0.57735,0.57735;2.0944rad)
  sketch-geometry (29):
    g0: LineSegment [constr] StartX=-12.6 StartY=-8e-16 StartZ=0 EndX=-12.6 EndY=-13.6 EndZ=0
    g1: GeomPoint [constr] X=-5.8 Y=-6.8 Z=0
    g2: LineSegment [constr] StartX=-10.3 StartY=-9.6 StartZ=0 EndX=-10.3 EndY=-12.6 EndZ=0
    g3: LineSegment [constr] StartX=-10.3 StartY=-12.6 StartZ=0 EndX=-1.3 EndY=-12.6 EndZ=0
    g4: LineSegment [constr] StartX=-1.3 StartY=-12.6 StartZ=0 EndX=-1.3 EndY=-9.6 EndZ=0
    g5: LineSegment [constr] StartX=-1.3 StartY=-9.6 StartZ=0 EndX=-10.3 EndY=-9.6 EndZ=0
    g6: LineSegment [constr] StartX=-10.3 StartY=-1 StartZ=0 EndX=-10.3 EndY=-4 EndZ=0
    g7: LineSegment [constr] StartX=-10.3 StartY=-4 StartZ=0 EndX=-1.3 EndY=-4 EndZ=0
    g8: LineSegment [constr] StartX=-1.3 StartY=-4 StartZ=0 EndX=-1.3 EndY=-1 EndZ=0
    g9: LineSegment [constr] StartX=-1.3 StartY=-1 StartZ=0 EndX=-10.3 EndY=-1 EndZ=0
    g10: LineSegment [constr] StartX=-7.3 StartY=-4 StartZ=0 EndX=-7.3 EndY=-9.6 EndZ=0
    g11: LineSegment [constr] StartX=-7.3 StartY=-9.6 StartZ=0 EndX=-4.3 EndY=-9.6 EndZ=0
    g12: LineSegment [constr] StartX=-4.3 StartY=-9.6 StartZ=0 EndX=-4.3 EndY=-4 EndZ=0
    g13: LineSegment [constr] StartX=-4.3 StartY=-4 StartZ=0 EndX=-7.3 EndY=-4 EndZ=0
    g14: GeomPoint [constr] X=-5.8 Y=-4 Z=0
    g15: GeomPoint [constr] X=-5.8 Y=-9.6 Z=0
    g16: GeomPoint [constr] X=-5.8 Y=-6.8 Z=0
    g17: LineSegment StartX=-10.3 StartY=-1 StartZ=0 EndX=-1.3 EndY=-1 EndZ=0
    g18: LineSegment StartX=-1.3 StartY=-1 StartZ=0 EndX=-1.3 EndY=-4 EndZ=0
    g19: LineSegment StartX=-1.3 StartY=-4 StartZ=0 EndX=-4.3 EndY=-4 EndZ=0
    g20: LineSegment StartX=-4.3 StartY=-4 StartZ=0 EndX=-4.3 EndY=-9.6 EndZ=0
    g21: LineSegment StartX=-4.3 StartY=-9.6 StartZ=0 EndX=-1.3 EndY=-9.6 EndZ=0
    g22: LineSegment StartX=-1.3 StartY=-9.6 StartZ=0 EndX=-1.3 EndY=-12.6 EndZ=0
    g23: LineSegment StartX=-1.3 StartY=-12.6 StartZ=0 EndX=-10.3 EndY=-12.6 EndZ=0
    g24: LineSegment StartX=-10.3 StartY=-12.6 StartZ=0 EndX=-10.3 EndY=-9.6 EndZ=0
    g25: LineSegment StartX=-10.3 StartY=-9.6 StartZ=0 EndX=-7.3 EndY=-9.6 EndZ=0
    g26: LineSegment StartX=-7.3 StartY=-9.6 StartZ=0 EndX=-7.3 EndY=-4 EndZ=0
    g27: LineSegment StartX=-7.3 StartY=-4 StartZ=0 EndX=-10.3 EndY=-4 EndZ=0
    g28: LineSegment StartX=-10.3 StartY=-4 StartZ=0 EndX=-10.3 EndY=-1 EndZ=0
  constraints (64):
    c: Coincident(g0,g-9)
    c: PointOnObject(g0,g-3)
    c: Vertical(g0)
    c: Symmetric(g0,g-6,g1)
    c: Coincident(g2,g3)
    c: Coincident(g3,g4)
    c: Coincident(g4,g5)
    c: Coincident(g5,g2)
    c: Vertical(g2)
    c: Vertical(g4)
    c: Horizontal(g3)
    c: Horizontal(g5)
    c: Distance(g2,g4) = 9
    c: Distance(g3,g5) = 3
    c: Coincident(g6,g7)
    c: Coincident(g7,g8)
    c: Coincident(g8,g9)
    c: Coincident(g9,g6)
    c: Vertical(g6)
    c: Vertical(g8)
    c: Horizontal(g7)
    c: Horizontal(g9)
    c: Distance(g6,g8) = 9
    c: Distance(g7,g9) = 3
    c: Coincident(g10,g11)
    c: Coincident(g11,g12)
    c: Coincident(g12,g13)
    c: Coincident(g13,g10)
    c: Vertical(g10)
    c: Vertical(g12)
    c: Horizontal(g11)
    c: Horizontal(g13)
    c: Distance(g10,g12) = 3
    c: Distance(g11,g13) = 5.6
    c: Symmetric(g6,g7,g14)
    c: Symmetric(g10,g12,g14)
    c: Symmetric(g10,g11,g15)
    c: Symmetric(g2,g4,g15)
    c: Symmetric(g10,g12,g16)
    c: Coincident(g16,g1)
    c: Coincident(g17,g6)
    c: Coincident(g17,g8)
    c: Coincident(g18,g8)
    c: Coincident(g18,g7)
    c: Coincident(g19,g7)
    c: Coincident(g19,g12)
    c: Coincident(g20,g12)
    c: Coincident(g20,g11)
    c: Coincident(g21,g11)
    c: Coincident(g21,g4)
    c: Coincident(g22,g4)
    c: Coincident(g22,g3)
    c: Coincident(g23,g3)
    c: Coincident(g23,g2)
    c: Coincident(g24,g2)
    c: Coincident(g24,g2)
    c: Coincident(g25,g2)
    c: Coincident(g25,g10)
    c: Coincident(g26,g10)
    c: Coincident(g26,g10)
    c: Coincident(g27,g10)
    c: Coincident(g27,g6)
    c: Coincident(g28,g6)
    c: Coincident(g28,g6)
FEATURE [PartDesign::Pocket] Pocket
  BaseFeature = -> Pad020
  Direction = (-1,0,0)
  Length = 5
  Length2 = 5
  Profile = -> Sketch017
  ReferenceAxis = -> Sketch017 [N_Axis]
  Refine = true
  SideType = 0
  Suppressed = false
  Type = 1
  Type2 = 0
FEATURE [PartDesign::Fillet] Fillet019
  Base = -> Pocket [Edge143,Face60,Edge123,Edge122,Edge139,Edge137,Edge141,Edge129,Edge135,Edge131,Edge133,Edge125,Edge127,Edge156,Face61,Edge152,Edge150,Edge148,Edge154,Edge164,Edge145,Edge146,Edge166,Edge158,Edge162,Edge160,Face35,Edge58,Edge59,Edge79,Edge77,Edge75,Edge73,Edge71,Edge69,Edge61,Edge119,Edge118,Edge117,Edge116,+11 more]
  BaseFeature = -> Pocket
  Radius = 1
  Refine = true
  SupportTransform = false
  Suppressed = false
  UseAllEdges = false
FEATURE [PartDesign::Fillet] Fillet020
  Base = -> Fillet019 [Face29,Face28,Face82,Face81,Face79,Face27,Face26,Face54,Face80,Face1]
  BaseFeature = -> Fillet019
  Radius = 0.45
  Refine = true
  SupportTransform = false
  Suppressed = false
  UseAllEdges = false
FEATURE [PartDesign::Body] Body006  label="ConnectorSlidingT"
  AllowCompound = true
  Group = -> [Binder011,Sketch014,Pad017,Sketch015,Pad018,Sketch016,Pad019,Pad020,Sketch017,Pocket,Fillet019,Fillet020]
  Origin = -> Origin026
  Tip = -> Fillet020
FEATURE [PartDesign::Pad] Pad015
  Direction = (0,0,1)
  Length = 35
  Length2 = 10
  Profile = -> Binder009
  Refine = true
  SideType = 0
  Suppressed = false
  Type = 0
  Type2 = 0
FEATURE [PartDesign::Fillet] Fillet
  Base = -> Fillet012 [Face217,Face243,Face168,Face242]
  BaseFeature = -> Fillet012
  Radius = 1
  Refine = true
  SupportTransform = false
  Suppressed = false
  UseAllEdges = false
FEATURE [PartDesign::Fillet] Fillet021
  Base = -> Fillet [Edge183,Edge181,Face85,Face87,Face80,Face82,Face86,Face89,Face94,Face93,Face81,Face79,Face95]
  BaseFeature = -> Fillet
  Radius = 0.25
  Refine = true
  SupportTransform = false
  Suppressed = false
  UseAllEdges = false
FEATURE [PartDesign::Body] Body002  label="Connector4WayCross"
  AllowCompound = true
  Group = -> [Binder006,Pad008,Pad009,Binder007,Pad010,Sketch009,Pad012,Sketch010,Pad013,Fillet010,Fillet011,Fillet012,Fillet,Fillet021]
  Origin = -> Origin012
  Tip = -> Fillet021
FEATURE [PartDesign::Fillet] Fillet017
  Base = -> Pad015
  BaseFeature = -> Pad015
  Radius = 0.5
  Refine = true
  SupportTransform = false
  Suppressed = false
  UseAllEdges = true
FEATURE [PartDesign::Body] Body004  label="Rail35mm"
  AllowCompound = true
  Group = -> [Pad015,Fillet017,Binder009]
  Origin = -> Origin018
  Tip = -> Fillet017
FEATURE [PartDesign::SubShapeBinder] Binder012
  BindCopyOnChange = 0
  BindMode = 0
  ClaimChildren = false
  Context = -> Body007 [Binder012.]
  Fuse = false
  MakeFace = true
  OffsetFill = false
  OffsetIntersection = false
  OffsetJoinType = 0
  OffsetOpenResult = false
  PartialLoad = false
  Refine = true
  Relative = true
  Support = -> [Sketch]
  _Version = 2
FEATURE [App::Point] Origin029  label="Origin031"
  Role = Origin
FEATURE [Sketcher::SketchObject] Sketch018
  ArcFitTolerance = 1e-06
  AttachmentSupport = -> [Origin028]
  ExternalGeometry = -> [Binder012]
  ExternalTypes = [0]
  FullyConstrained = true
  MakeInternals = false
  MapMode = 5
FEATURE [PartDesign::Pad] Pad021
  Direction = (0,0,1)
  Length = 10
  Length2 = 10
  Profile = -> Sketch018
  ReferenceAxis = -> Sketch018 [N_Axis]
  Refine = true
  SideType = 0
  Suppressed = false
  Type = 0
  Type2 = 0
FEATURE [Sketcher::SketchObject] Sketch019
  ArcFitTolerance = 1e-06
  AttachmentSupport = -> [Origin028]
  ExternalGeometry = -> [Pad021]
  ExternalTypes = [0,0,0,0]
  FullyConstrained = true
  MakeInternals = false
  MapMode = 5
FEATURE [PartDesign::Pad] Pad022
  BaseFeature = -> Pad021
  Direction = (0,0,1)
  Length = 13.6
  Length2 = 10
  Profile = -> Sketch019
  ReferenceAxis = -> Sketch019 [N_Axis]
  Refine = true
  Reversed = true
  SideType = 0
  Suppressed = false
  Type = 0
  Type2 = 0
  expr: Length = 2 + 3 + 3 + 5.6
FEATURE [Sketcher::SketchObject] Sketch020
  ArcFitTolerance = 1e-06
  AttachmentOffset = pos=(0,0,-1) rot=(0,0,1;0rad)
  AttachmentSupport = -> [Origin028]
  ExternalGeometry = -> [Pad022]
  ExternalTypes = [0]
  FullyConstrained = true
  MakeInternals = false
  MapMode = 5
  Placement = pos=(0,1,-2e-16) rot=(1,0,0;1.5708rad)
  sketch-geometry (32):
    g0: LineSegment [constr] StartX=10 StartY=-3.6e-15 StartZ=0 EndX=-1 EndY=-3.6e-15 EndZ=0
    g1: LineSegment [constr] StartX=-5.3071e-12 StartY=-1 StartZ=0 EndX=-5.3071e-12 EndY=-4 EndZ=0
    g2: LineSegment [constr] StartX=-5.3071e-12 StartY=-4 StartZ=0 EndX=9 EndY=-4 EndZ=0
    g3: LineSegment [constr] StartX=9 StartY=-4 StartZ=0 EndX=9 EndY=-1 EndZ=0
    g4: LineSegment [constr] StartX=9 StartY=-1 StartZ=0 EndX=-5.3078e-12 EndY=-1 EndZ=0
    g5: LineSegment [constr] StartX=-5.3078e-12 StartY=-9.6 StartZ=0 EndX=-5.3078e-12 EndY=-12.6 EndZ=0
    g6: LineSegment [constr] StartX=-5.3078e-12 StartY=-12.6 StartZ=0 EndX=9 EndY=-12.6 EndZ=0
    g7: LineSegment [constr] StartX=9 StartY=-12.6 StartZ=0 EndX=9 EndY=-9.6 EndZ=0
    g8: LineSegment [constr] StartX=9 StartY=-9.6 StartZ=0 EndX=-5.3078e-12 EndY=-9.6 EndZ=0
    g9: LineSegment [constr] StartX=3 StartY=-4 StartZ=0 EndX=3 EndY=-9.6 EndZ=0
    g10: LineSegment [constr] StartX=3 StartY=-9.6 StartZ=0 EndX=6 EndY=-9.6 EndZ=0
    g11: LineSegment [constr] StartX=6 StartY=-9.6 StartZ=0 EndX=6 EndY=-4 EndZ=0
    g12: LineSegment [constr] StartX=6 StartY=-4 StartZ=0 EndX=3 EndY=-4 EndZ=0
    g13: GeomPoint [constr] X=4.5 Y=-4 Z=0
    g14: GeomPoint [constr] X=4.5 Y=-6.8 Z=0
    g15: GeomPoint [constr] X=4.5 Y=-9.6 Z=0
    g16: LineSegment StartX=-1 StartY=-3.6e-15 StartZ=0 EndX=-1 EndY=-13.6 EndZ=0
    g17: LineSegment StartX=-1 StartY=-13.6 StartZ=0 EndX=10 EndY=-13.6 EndZ=0
    g18: LineSegment StartX=10 StartY=-13.6 StartZ=0 EndX=10 EndY=-3.6e-15 EndZ=0
    g19: LineSegment StartX=10 StartY=-3.6e-15 StartZ=0 EndX=-1 EndY=-3.6e-15 EndZ=0
    g20: LineSegment StartX=-5.3071e-12 StartY=-1 StartZ=0 EndX=9 EndY=-1 EndZ=0
    g21: LineSegment StartX=9 StartY=-1 StartZ=0 EndX=9 EndY=-4 EndZ=0
    g22: LineSegment StartX=9 StartY=-4 StartZ=0 EndX=6 EndY=-4 EndZ=0
    g23: LineSegment StartX=6 StartY=-4 StartZ=0 EndX=6 EndY=-9.6 EndZ=0
    g24: LineSegment StartX=6 StartY=-9.6 StartZ=0 EndX=9 EndY=-9.6 EndZ=0
    g25: LineSegment StartX=9 StartY=-9.6 StartZ=0 EndX=9 EndY=-12.6 EndZ=0
    g26: LineSegment StartX=9 StartY=-12.6 StartZ=0 EndX=-5.3078e-12 EndY=-12.6 EndZ=0
    g27: LineSegment StartX=-5.3078e-12 StartY=-12.6 StartZ=0 EndX=-5.3078e-12 EndY=-9.6 EndZ=0
    g28: LineSegment StartX=-5.3078e-12 StartY=-9.6 StartZ=0 EndX=3 EndY=-9.6 EndZ=0
    g29: LineSegment StartX=3 StartY=-9.6 StartZ=0 EndX=3 EndY=-4 EndZ=0
    g30: LineSegment StartX=3 StartY=-4 StartZ=0 EndX=-5.3073e-12 EndY=-4 EndZ=0
    g31: LineSegment StartX=-5.3071e-12 StartY=-4 StartZ=0 EndX=-5.3071e-12 EndY=-1 EndZ=0
  constraints (74):
    c: Horizontal(g0)
    c: PointOnObject(g0,g-3)
    c: PointOnObject(g0,g-5)
    c: Distance(g-6,g0) = 10
    c: Coincident(g1,g2)
    c: Coincident(g2,g3)
    c: Coincident(g3,g4)
    c: Coincident(g4,g1)
    c: Vertical(g1)
    c: Vertical(g3)
    c: Horizontal(g2)
    c: Horizontal(g4)
    c: Distance(g1,g3) = 9
    c: Distance(g2,g4) = 3
    c: Coincident(g5,g6)
    c: Coincident(g6,g7)
    c: Coincident(g7,g8)
    c: Coincident(g8,g5)
    c: Vertical(g5)
    c: Vertical(g7)
    c: Horizontal(g6)
    c: Horizontal(g8)
    c: Distance(g5,g7) = 9
    c: Distance(g6,g8) = 3
    c: Coincident(g9,g10)
    c: Coincident(g10,g11)
    c: Coincident(g11,g12)
    c: Coincident(g12,g9)
    c: Vertical(g9)
    c: Vertical(g11)
    c: Horizontal(g10)
    c: Horizontal(g12)
    c: Distance(g9,g11) = 3
    c: Distance(g10,g12) = 5.6
    c: Symmetric(g5,g7,g15)
    c: Symmetric(g9,g10,g15)
    c: Symmetric(g1,g2,g13)
    c: Symmetric(g9,g11,g13)
    c: Symmetric(g9,g11,g14)
    c: Symmetric(g-4,g0,g14)
    c: Coincident(g16,g17)
    c: Coincident(g17,g18)
    c: Coincident(g18,g19)
    c: Coincident(g19,g16)
    c: Vertical(g16)
    c: Vertical(g18)
    c: Horizontal(g17)
    c: Horizontal(g19)
    c: Coincident(g16,g0)
    c: Coincident(g17,g-5)
    c: Coincident(g20,g1)
    c: Coincident(g20,g3)
    c: Coincident(g21,g3)
    c: Coincident(g21,g2)
    c: Coincident(g22,g2)
    c: Coincident(g22,g11)
    c: Coincident(g23,g11)
    c: Coincident(g23,g10)
    c: Coincident(g24,g10)
    c: Coincident(g24,g7)
    c: Coincident(g25,g7)
    c: Coincident(g25,g6)
    c: Coincident(g26,g6)
    c: Coincident(g26,g5)
    c: Coincident(g27,g5)
    c: Coincident(g27,g5)
    c: Coincident(g28,g5)
    c: Coincident(g28,g9)
    c: Coincident(g29,g9)
    c: Coincident(g29,g9)
    c: Coincident(g30,g9)
    c: Coincident(g30,g1)
    c: Coincident(g31,g1)
    c: Coincident(g31,g1)
FEATURE [PartDesign::Pad] Pad023
  BaseFeature = -> Pad022
  Direction = (0,-1,2e-16)
  Length = 10
  Length2 = 10
  Profile = -> Sketch020
  ReferenceAxis = -> Sketch020 [N_Axis]
  Refine = true
  Reversed = true
  SideType = 0
  Suppressed = false
  Type = 0
  Type2 = 0
FEATURE [Sketcher::SketchObject] Sketch021
  ArcFitTolerance = 1e-06
  ExternalTypes = [0]
  FullyConstrained = true
  MakeInternals = false
  MapMode = 5
  Placement = pos=(10,0,0) rot=(0.57735,0.57735,0.57735;2.0944rad)
  sketch-geometry (29):
    g0: LineSegment [constr] StartX=-12.6 StartY=-8e-16 StartZ=0 EndX=-12.6 EndY=-13.6 EndZ=0
    g1: GeomPoint [constr] X=-5.8 Y=-6.8 Z=0
    g2: LineSegment [constr] StartX=-10.3 StartY=-9.6 StartZ=0 EndX=-10.3 EndY=-12.6 EndZ=0
    g3: LineSegment [constr] StartX=-10.3 StartY=-12.6 StartZ=0 EndX=-1.3 EndY=-12.6 EndZ=0
    g4: LineSegment [constr] StartX=-1.3 StartY=-12.6 StartZ=0 EndX=-1.3 EndY=-9.6 EndZ=0
    g5: LineSegment [constr] StartX=-1.3 StartY=-9.6 StartZ=0 EndX=-10.3 EndY=-9.6 EndZ=0
    g6: LineSegment [constr] StartX=-10.3 StartY=-1 StartZ=0 EndX=-10.3 EndY=-4 EndZ=0
    g7: LineSegment [constr] StartX=-10.3 StartY=-4 StartZ=0 EndX=-1.3 EndY=-4 EndZ=0
    g8: LineSegment [constr] StartX=-1.3 StartY=-4 StartZ=0 EndX=-1.3 EndY=-1 EndZ=0
    g9: LineSegment [constr] StartX=-1.3 StartY=-1 StartZ=0 EndX=-10.3 EndY=-1 EndZ=0
    g10: LineSegment [constr] StartX=-7.3 StartY=-4 StartZ=0 EndX=-7.3 EndY=-9.6 EndZ=0
    g11: LineSegment [constr] StartX=-7.3 StartY=-9.6 StartZ=0 EndX=-4.3 EndY=-9.6 EndZ=0
    g12: LineSegment [constr] StartX=-4.3 StartY=-9.6 StartZ=0 EndX=-4.3 EndY=-4 EndZ=0
    g13: LineSegment [constr] StartX=-4.3 StartY=-4 StartZ=0 EndX=-7.3 EndY=-4 EndZ=0
    g14: GeomPoint [constr] X=-5.8 Y=-4 Z=0
    g15: GeomPoint [constr] X=-5.8 Y=-9.6 Z=0
    g16: GeomPoint [constr] X=-5.8 Y=-6.8 Z=0
    g17: LineSegment StartX=-10.3 StartY=-1 StartZ=0 EndX=-1.3 EndY=-1 EndZ=0
    g18: LineSegment StartX=-1.3 StartY=-1 StartZ=0 EndX=-1.3 EndY=-4 EndZ=0
    g19: LineSegment StartX=-1.3 StartY=-4 StartZ=0 EndX=-4.3 EndY=-4 EndZ=0
    g20: LineSegment StartX=-4.3 StartY=-4 StartZ=0 EndX=-4.3 EndY=-9.6 EndZ=0
    g21: LineSegment StartX=-4.3 StartY=-9.6 StartZ=0 EndX=-1.3 EndY=-9.6 EndZ=0
    g22: LineSegment StartX=-1.3 StartY=-9.6 StartZ=0 EndX=-1.3 EndY=-12.6 EndZ=0
    g23: LineSegment StartX=-1.3 StartY=-12.6 StartZ=0 EndX=-10.3 EndY=-12.6 EndZ=0
    g24: LineSegment StartX=-10.3 StartY=-12.6 StartZ=0 EndX=-10.3 EndY=-9.6 EndZ=0
    g25: LineSegment StartX=-10.3 StartY=-9.6 StartZ=0 EndX=-7.3 EndY=-9.6 EndZ=0
    g26: LineSegment StartX=-7.3 StartY=-9.6 StartZ=0 EndX=-7.3 EndY=-4 EndZ=0
    g27: LineSegment StartX=-7.3 StartY=-4 StartZ=0 EndX=-10.3 EndY=-4 EndZ=0
    g28: LineSegment StartX=-10.3 StartY=-4 StartZ=0 EndX=-10.3 EndY=-1 EndZ=0
  constraints (64):
    c: Coincident(g0,g-9)
    c: PointOnObject(g0,g-3)
    c: Vertical(g0)
    c: Symmetric(g0,g-6,g1)
    c: Coincident(g2,g3)
    c: Coincident(g3,g4)
    c: Coincident(g4,g5)
    c: Coincident(g5,g2)
    c: Vertical(g2)
    c: Vertical(g4)
    c: Horizontal(g3)
    c: Horizontal(g5)
    c: Distance(g2,g4) = 9
    c: Distance(g3,g5) = 3
    c: Coincident(g6,g7)
    c: Coincident(g7,g8)
    c: Coincident(g8,g9)
    c: Coincident(g9,g6)
    c: Vertical(g6)
    c: Vertical(g8)
    c: Horizontal(g7)
    c: Horizontal(g9)
    c: Distance(g6,g8) = 9
    c: Distance(g7,g9) = 3
    c: Coincident(g10,g11)
    c: Coincident(g11,g12)
    c: Coincident(g12,g13)
    c: Coincident(g13,g10)
    c: Vertical(g10)
    c: Vertical(g12)
    c: Horizontal(g11)
    c: Horizontal(g13)
    c: Distance(g10,g12) = 3
    c: Distance(g11,g13) = 5.6
    c: Symmetric(g6,g7,g14)
    c: Symmetric(g10,g12,g14)
    c: Symmetric(g10,g11,g15)
    c: Symmetric(g2,g4,g15)
    c: Symmetric(g10,g12,g16)
    c: Coincident(g16,g1)
    c: Coincident(g17,g6)
    c: Coincident(g17,g8)
    c: Coincident(g18,g8)
    c: Coincident(g18,g7)
    c: Coincident(g19,g7)
    c: Coincident(g19,g12)
    c: Coincident(g20,g12)
    c: Coincident(g20,g11)
    c: Coincident(g21,g11)
    c: Coincident(g21,g4)
    c: Coincident(g22,g4)
    c: Coincident(g22,g3)
    c: Coincident(g23,g3)
    c: Coincident(g23,g2)
    c: Coincident(g24,g2)
    c: Coincident(g24,g2)
    c: Coincident(g25,g2)
    c: Coincident(g25,g10)
    c: Coincident(g26,g10)
    c: Coincident(g26,g10)
    c: Coincident(g27,g10)
    c: Coincident(g27,g6)
    c: Coincident(g28,g6)
    c: Coincident(g28,g6)
FEATURE [PartDesign::Pocket] Pocket001
  BaseFeature = -> Pad023
  Direction = (-1,0,0)
  Length = 5
  Length2 = 5
  Profile = -> Sketch021
  ReferenceAxis = -> Sketch021 [N_Axis]
  Refine = true
  SideType = 0
  Suppressed = false
  Type = 1
  Type2 = 0
FEATURE [App::Point] Origin030  label="Origin032"
  Role = Origin
FEATURE [Sketcher::SketchObject] Sketch040  label="SketchPowerDistroBlock"
  ArcFitTolerance = 1e-06
  AttachmentSupport = -> [Origin031]
  ExternalTypes = [0]
  FullyConstrained = true
  MakeInternals = false
  MapMode = 5
  expr: Constraints[14] = 88 / 2
  expr: Constraints[15] = 88 / 2
  sketch-geometry (9):
    g0: LineSegment StartX=-49 StartY=-5 StartZ=0 EndX=49 EndY=-5 EndZ=0
    g1: LineSegment StartX=49 StartY=-5 StartZ=0 EndX=49 EndY=5 EndZ=0
    g2: LineSegment StartX=49 StartY=5 StartZ=0 EndX=-49 EndY=5 EndZ=0
    g3: LineSegment StartX=-49 StartY=5 StartZ=0 EndX=-49 EndY=-5 EndZ=0
    g4: GeomPoint [constr] X=0 Y=0 Z=0
    g5: GeomPoint X=-44 Y=0 Z=0
    g6: GeomPoint X=44 Y=0 Z=0
    g7: Circle CenterX=-44 CenterY=0 CenterZ=0 NormalX=0 NormalY=0 NormalZ=1 AngleXU=0 Radius=2
    g8: Circle CenterX=44 CenterY=0 CenterZ=0 NormalX=0 NormalY=0 NormalZ=1 AngleXU=0 Radius=2
  constraints (20):
    c: Coincident(g0,g1)
    c: Coincident(g1,g2)
    c: Coincident(g2,g3)
    c: Coincident(g3,g0)
    c: Horizontal(g0)
    c: Horizontal(g2)
    c: Vertical(g1)
    c: Vertical(g3)
    c: Symmetric(g2,g0,g4)
    c: Distance(g1,g3) = 98
    c: Distance(g0,g2) = 10
    c: Coincident(g4,g-1)
    c: PointOnObject(g5,g-1)
    c: PointOnObject(g6,g-1)
    c: DistanceX(g5,g4) = 44
    c: DistanceX(g4,g6) = 44
    c: Diameter(g7) = 4
    c: Coincident(g7,g5)
    c: Diameter(g8) = 4
    c: Coincident(g8,g6)
FEATURE [PartDesign::Pad] Pad024
  Direction = (0,0,1)
  Length = 13.6
  Length2 = 10
  Profile = -> Sketch040
  ReferenceAxis = -> Sketch040 [N_Axis]
  Refine = true
  SideType = 0
  Suppressed = false
  Type = 0
  Type2 = 0
  expr: Length = 3 + 5.6 + 3 + 2
FEATURE [Sketcher::SketchObject] Sketch041
  ArcFitTolerance = 1e-06
  AttachmentSupport = -> [Pad024]
  ExternalGeometry = -> [Pad024]
  ExternalTypes = [0]
  FullyConstrained = true
  MakeInternals = false
  MapMode = 5
  Placement = pos=(0,-5,0) rot=(1,0,0;1.5708rad)
  sketch-geometry (27):
    g0: GeomPoint [constr] X=1.7e-15 Y=6.8 Z=0
    g1: LineSegment [constr] StartX=-4.5 StartY=12.6 StartZ=0 EndX=-4.5 EndY=9.6 EndZ=0
    g2: LineSegment [constr] StartX=-4.5 StartY=9.6 StartZ=0 EndX=4.5 EndY=9.6 EndZ=0
    g3: LineSegment [constr] StartX=4.5 StartY=9.6 StartZ=0 EndX=4.5 EndY=12.6 EndZ=0
    g4: LineSegment [constr] StartX=4.5 StartY=12.6 StartZ=0 EndX=-4.5 EndY=12.6 EndZ=0
    g5: LineSegment [constr] StartX=1.5 StartY=9.6 StartZ=0 EndX=1.5 EndY=4 EndZ=0
    g6: LineSegment [constr] StartX=1.5 StartY=4 StartZ=0 EndX=-1.5 EndY=4 EndZ=0
    g7: LineSegment [constr] StartX=-1.5 StartY=4 StartZ=0 EndX=-1.5 EndY=9.6 EndZ=0
    g8: LineSegment [constr] StartX=-1.5 StartY=9.6 StartZ=0 EndX=1.5 EndY=9.6 EndZ=0
    g9: LineSegment [constr] StartX=-4.5 StartY=4 StartZ=0 EndX=-4.5 EndY=1 EndZ=0
    g10: LineSegment [constr] StartX=-4.5 StartY=1 StartZ=0 EndX=4.5 EndY=1 EndZ=0
    g11: LineSegment [constr] StartX=4.5 StartY=1 StartZ=0 EndX=4.5 EndY=4 EndZ=0
    g12: LineSegment [constr] StartX=4.5 StartY=4 StartZ=0 EndX=-4.5 EndY=4 EndZ=0
    g13: GeomPoint [constr] X=2.1e-15 Y=9.6 Z=0
    g14: GeomPoint [constr] X=2.1e-15 Y=4 Z=0
    g15: LineSegment StartX=-4.5 StartY=12.6 StartZ=0 EndX=4.5 EndY=12.6 EndZ=0
    g16: LineSegment StartX=4.5 StartY=12.6 StartZ=0 EndX=4.5 EndY=9.6 EndZ=0
    g17: LineSegment StartX=4.5 StartY=9.6 StartZ=0 EndX=1.5 EndY=9.6 EndZ=0
    g18: LineSegment StartX=1.5 StartY=9.6 StartZ=0 EndX=1.5 EndY=4 EndZ=0
    g19: LineSegment StartX=1.5 StartY=4 StartZ=0 EndX=4.5 EndY=4 EndZ=0
    g20: LineSegment StartX=4.5 StartY=4 StartZ=0 EndX=4.5 EndY=1 EndZ=0
    g21: LineSegment StartX=4.5 StartY=1 StartZ=0 EndX=-4.5 EndY=1 EndZ=0
    g22: LineSegment StartX=-4.5 StartY=1 StartZ=0 EndX=-4.5 EndY=4 EndZ=0
    g23: LineSegment StartX=-4.5 StartY=4 StartZ=0 EndX=-1.5 EndY=4 EndZ=0
    g24: LineSegment StartX=-1.5 StartY=4 StartZ=0 EndX=-1.5 EndY=9.6 EndZ=0
    g25: LineSegment StartX=-1.5 StartY=9.6 StartZ=0 EndX=-4.5 EndY=9.6 EndZ=0
    g26: LineSegment StartX=-4.5 StartY=9.6 StartZ=0 EndX=-4.5 EndY=12.6 EndZ=0
  constraints (60):
    c: Symmetric(g-5,g-6,g0)
    c: Coincident(g1,g2)
    c: Coincident(g2,g3)
    c: Coincident(g3,g4)
    c: Coincident(g4,g1)
    c: Vertical(g1)
    c: Vertical(g3)
    c: Horizontal(g2)
    c: Horizontal(g4)
    c: Distance(g1,g3) = 9
    c: Distance(g2,g4) = 3
    c: Coincident(g5,g6)
    c: Coincident(g6,g7)
    c: Coincident(g7,g8)
    c: Coincident(g8,g5)
    c: Vertical(g5)
    c: Vertical(g7)
    c: Horizontal(g6)
    c: Horizontal(g8)
    c: Distance(g5,g7) = 3
    c: Distance(g6,g8) = 5.6
    c: Coincident(g9,g10)
    c: Coincident(g10,g11)
    c: Coincident(g11,g12)
    c: Coincident(g12,g9)
    c: Vertical(g9)
    c: Vertical(g11)
    c: Horizontal(g10)
    c: Horizontal(g12)
    c: Distance(g9,g11) = 9
    c: Distance(g10,g12) = 3
    c: Symmetric(g1,g2,g13)
    c: Symmetric(g5,g7,g13)
    c: Symmetric(g9,g11,g14)
    c: Symmetric(g5,g6,g14)
    c: Symmetric(g5,g7,g0)
    c: Coincident(g15,g1)
    c: Coincident(g15,g3)
    c: Coincident(g16,g3)
    c: Coincident(g16,g2)
    c: Coincident(g17,g2)
    c: Coincident(g17,g5)
    c: Coincident(g18,g5)
    c: Coincident(g18,g5)
    c: Coincident(g19,g5)
    c: Coincident(g19,g11)
    c: Coincident(g20,g11)
    c: Coincident(g20,g10)
    c: Coincident(g21,g10)
    c: Coincident(g21,g9)
    c: Coincident(g22,g9)
    c: Coincident(g22,g9)
    c: Coincident(g23,g9)
    c: Coincident(g23,g6)
    c: Coincident(g24,g6)
    c: Coincident(g24,g7)
    c: Coincident(g25,g7)
    c: Coincident(g25,g1)
    c: Coincident(g26,g1)
    c: Coincident(g26,g1)
FEATURE [PartDesign::Pocket] Pocket029
  BaseFeature = -> Pad024
  Direction = (0,1,-2e-16)
  Length = 5
  Length2 = 5
  Profile = -> Sketch041
  ReferenceAxis = -> Sketch041 [N_Axis]
  Refine = true
  SideType = 0
  Suppressed = false
  Type = 1
  Type2 = 0
FEATURE [PartDesign::Hole] Hole013
  BaseFeature = -> Pocket029
  BaseProfileType = 7
  CustomThreadClearance = 0
  Depth = 25
  DepthType = 0
  Diameter = 3.7
  DrillForDepth = false
  DrillPoint = 1
  DrillPointAngle = 118
  HoleCutCountersinkAngle = 90
  HoleCutCustomValues = false
  HoleCutDepth = 0
  HoleCutDiameter = 0
  HoleCutType = 0
  ModelThread = false
  Profile = -> Pocket029 [Edge26,Edge27]
  Refine = true
  Suppressed = false
  Tapered = false
  TaperedAngle = 90
  ThreadClass = 0
  ThreadDepth = 25
  ThreadDepthType = 0
  ThreadDiameter = 4.5
  ThreadDirection = 0
  ThreadFit = 0
  ThreadSize = 12
  ThreadType = 1
  Threaded = true
  UseCustomThreadClearance = false
FEATURE [PartDesign::Fillet] Fillet024
  Base = -> Hole013 [Edge32,Edge29,Edge31,Edge50,Edge48,Edge34,Edge46,Edge36,Edge38,Edge40,Edge42,Edge44,Edge14,Edge49,Edge8,Edge37,Edge9,Edge13,Edge10,Edge12]
  BaseFeature = -> Hole013
  Radius = 1
  Refine = true
  SupportTransform = false
  Suppressed = false
  UseAllEdges = false
FEATURE [PartDesign::Fillet] Fillet025
  Base = -> Fillet024 [Edge1,Edge27,Edge70]
  BaseFeature = -> Fillet024
  Radius = 0.9
  Refine = true
  SupportTransform = false
  Suppressed = false
  UseAllEdges = false
FEATURE [PartDesign::Fillet] Fillet026
  Base = -> Fillet025 [Face22,Face25]
  BaseFeature = -> Fillet025
  Radius = 0.5
  Refine = true
  SupportTransform = false
  Suppressed = false
  UseAllEdges = false
FEATURE [PartDesign::Fillet] Fillet027
  Base = -> Fillet026 [Face30,Face29]
  BaseFeature = -> Fillet026
  Radius = 1
  Refine = true
  SupportTransform = false
  Suppressed = false
  UseAllEdges = false
FEATURE [PartDesign::Body] Body010  label="RailMount88mm"
  AllowCompound = true
  Group = -> [Sketch040,Pad024,Sketch041,Pocket029,Hole013,Fillet024,Fillet025,Fillet026,Fillet027]
  Origin = -> Origin031
  Tip = -> Fillet027
FEATURE [App::Point] Origin032  label="Origin039"
  Role = Origin
FEATURE [Sketcher::SketchObject] Sketch047  label="SketchPowerDistroBlock001"
  ArcFitTolerance = 1e-06
  AttachmentSupport = -> [Origin033]
  ExternalTypes = [0]
  FullyConstrained = true
  MakeInternals = false
  MapMode = 5
  sketch-geometry (9):
    g0: LineSegment StartX=-45 StartY=-5 StartZ=0 EndX=45 EndY=-5 EndZ=0
    g1: LineSegment StartX=45 StartY=-5 StartZ=0 EndX=45 EndY=5 EndZ=0
    g2: LineSegment StartX=45 StartY=5 StartZ=0 EndX=-45 EndY=5 EndZ=0
    g3: LineSegment StartX=-45 StartY=5 StartZ=0 EndX=-45 EndY=-5 EndZ=0
    g4: GeomPoint [constr] X=0 Y=0 Z=0
    g5: GeomPoint X=-40 Y=0 Z=0
    g6: GeomPoint X=40 Y=0 Z=0
    g7: Circle CenterX=-40 CenterY=0 CenterZ=0 NormalX=0 NormalY=0 NormalZ=1 AngleXU=0 Radius=2
    g8: Circle CenterX=40 CenterY=0 CenterZ=0 NormalX=0 NormalY=0 NormalZ=1 AngleXU=0 Radius=2
  constraints (20):
    c: Coincident(g0,g1)
    c: Coincident(g1,g2)
    c: Coincident(g2,g3)
    c: Coincident(g3,g0)
    c: Horizontal(g0)
    c: Horizontal(g2)
    c: Vertical(g1)
    c: Vertical(g3)
    c: Symmetric(g2,g0,g4)
    c: Distance(g1,g3) = 90
    c: Distance(g0,g2) = 10
    c: Coincident(g4,g-1)
    c: PointOnObject(g5,g-1)
    c: PointOnObject(g6,g-1)
    c: DistanceX(g5,g4) = 40
    c: DistanceX(g4,g6) = 40
    c: Diameter(g7) = 4
    c: Coincident(g7,g5)
    c: Diameter(g8) = 4
    c: Coincident(g8,g6)
FEATURE [PartDesign::Pad] Pad025
  Direction = (0,0,1)
  Length = 13.6
  Length2 = 10
  Profile = -> Sketch047
  ReferenceAxis = -> Sketch047 [N_Axis]
  Refine = true
  SideType = 0
  Suppressed = false
  Type = 0
  Type2 = 0
  expr: Length = 3 + 5.6 + 3 + 2
FEATURE [Sketcher::SketchObject] Sketch048
  ArcFitTolerance = 1e-06
  AttachmentSupport = -> [Pad025]
  ExternalGeometry = -> [Pad025]
  ExternalTypes = [0]
  FullyConstrained = true
  MakeInternals = false
  MapMode = 5
  Placement = pos=(0,-5,0) rot=(1,0,0;1.5708rad)
  sketch-geometry (27):
    g0: GeomPoint [constr] X=1.7e-15 Y=6.8 Z=0
    g1: LineSegment [constr] StartX=-4.5 StartY=12.6 StartZ=0 EndX=-4.5 EndY=9.6 EndZ=0
    g2: LineSegment [constr] StartX=-4.5 StartY=9.6 StartZ=0 EndX=4.5 EndY=9.6 EndZ=0
    g3: LineSegment [constr] StartX=4.5 StartY=9.6 StartZ=0 EndX=4.5 EndY=12.6 EndZ=0
    g4: LineSegment [constr] StartX=4.5 StartY=12.6 StartZ=0 EndX=-4.5 EndY=12.6 EndZ=0
    g5: LineSegment [constr] StartX=1.5 StartY=9.6 StartZ=0 EndX=1.5 EndY=4 EndZ=0
    g6: LineSegment [constr] StartX=1.5 StartY=4 StartZ=0 EndX=-1.5 EndY=4 EndZ=0
    g7: LineSegment [constr] StartX=-1.5 StartY=4 StartZ=0 EndX=-1.5 EndY=9.6 EndZ=0
    g8: LineSegment [constr] StartX=-1.5 StartY=9.6 StartZ=0 EndX=1.5 EndY=9.6 EndZ=0
    g9: LineSegment [constr] StartX=-4.5 StartY=4 StartZ=0 EndX=-4.5 EndY=1 EndZ=0
    g10: LineSegment [constr] StartX=-4.5 StartY=1 StartZ=0 EndX=4.5 EndY=1 EndZ=0
    g11: LineSegment [constr] StartX=4.5 StartY=1 StartZ=0 EndX=4.5 EndY=4 EndZ=0
    g12: LineSegment [constr] StartX=4.5 StartY=4 StartZ=0 EndX=-4.5 EndY=4 EndZ=0
    g13: GeomPoint [constr] X=2.1e-15 Y=9.6 Z=0
    g14: GeomPoint [constr] X=2.1e-15 Y=4 Z=0
    g15: LineSegment StartX=-4.5 StartY=12.6 StartZ=0 EndX=4.5 EndY=12.6 EndZ=0
    g16: LineSegment StartX=4.5 StartY=12.6 StartZ=0 EndX=4.5 EndY=9.6 EndZ=0
    g17: LineSegment StartX=4.5 StartY=9.6 StartZ=0 EndX=1.5 EndY=9.6 EndZ=0
    g18: LineSegment StartX=1.5 StartY=9.6 StartZ=0 EndX=1.5 EndY=4 EndZ=0
    g19: LineSegment StartX=1.5 StartY=4 StartZ=0 EndX=4.5 EndY=4 EndZ=0
    g20: LineSegment StartX=4.5 StartY=4 StartZ=0 EndX=4.5 EndY=1 EndZ=0
    g21: LineSegment StartX=4.5 StartY=1 StartZ=0 EndX=-4.5 EndY=1 EndZ=0
    g22: LineSegment StartX=-4.5 StartY=1 StartZ=0 EndX=-4.5 EndY=4 EndZ=0
    g23: LineSegment StartX=-4.5 StartY=4 StartZ=0 EndX=-1.5 EndY=4 EndZ=0
    g24: LineSegment StartX=-1.5 StartY=4 StartZ=0 EndX=-1.5 EndY=9.6 EndZ=0
    g25: LineSegment StartX=-1.5 StartY=9.6 StartZ=0 EndX=-4.5 EndY=9.6 EndZ=0
    g26: LineSegment StartX=-4.5 StartY=9.6 StartZ=0 EndX=-4.5 EndY=12.6 EndZ=0
  constraints (60):
    c: Symmetric(g-5,g-6,g0)
    c: Coincident(g1,g2)
    c: Coincident(g2,g3)
    c: Coincident(g3,g4)
    c: Coincident(g4,g1)
    c: Vertical(g1)
    c: Vertical(g3)
    c: Horizontal(g2)
    c: Horizontal(g4)
    c: Distance(g1,g3) = 9
    c: Distance(g2,g4) = 3
    c: Coincident(g5,g6)
    c: Coincident(g6,g7)
    c: Coincident(g7,g8)
    c: Coincident(g8,g5)
    c: Vertical(g5)
    c: Vertical(g7)
    c: Horizontal(g6)
    c: Horizontal(g8)
    c: Distance(g5,g7) = 3
    c: Distance(g6,g8) = 5.6
    c: Coincident(g9,g10)
    c: Coincident(g10,g11)
    c: Coincident(g11,g12)
    c: Coincident(g12,g9)
    c: Vertical(g9)
    c: Vertical(g11)
    c: Horizontal(g10)
    c: Horizontal(g12)
    c: Distance(g9,g11) = 9
    c: Distance(g10,g12) = 3
    c: Symmetric(g1,g2,g13)
    c: Symmetric(g5,g7,g13)
    c: Symmetric(g9,g11,g14)
    c: Symmetric(g5,g6,g14)
    c: Symmetric(g5,g7,g0)
    c: Coincident(g15,g1)
    c: Coincident(g15,g3)
    c: Coincident(g16,g3)
    c: Coincident(g16,g2)
    c: Coincident(g17,g2)
    c: Coincident(g17,g5)
    c: Coincident(g18,g5)
    c: Coincident(g18,g5)
    c: Coincident(g19,g5)
    c: Coincident(g19,g11)
    c: Coincident(g20,g11)
    c: Coincident(g20,g10)
    c: Coincident(g21,g10)
    c: Coincident(g21,g9)
    c: Coincident(g22,g9)
    c: Coincident(g22,g9)
    c: Coincident(g23,g9)
    c: Coincident(g23,g6)
    c: Coincident(g24,g6)
    c: Coincident(g24,g7)
    c: Coincident(g25,g7)
    c: Coincident(g25,g1)
    c: Coincident(g26,g1)
    c: Coincident(g26,g1)
FEATURE [PartDesign::Pocket] Pocket036
  BaseFeature = -> Pad025
  Direction = (0,1,-2e-16)
  Length = 5
  Length2 = 5
  Profile = -> Sketch048
  ReferenceAxis = -> Sketch048 [N_Axis]
  Refine = true
  SideType = 0
  Suppressed = false
  Type = 1
  Type2 = 0
FEATURE [PartDesign::Hole] Hole015
  BaseFeature = -> Pocket036
  BaseProfileType = 7
  CustomThreadClearance = 0
  Depth = 25
  DepthType = 0
  Diameter = 3.7
  DrillForDepth = false
  DrillPoint = 1
  DrillPointAngle = 118
  HoleCutCountersinkAngle = 90
  HoleCutCustomValues = false
  HoleCutDepth = 0
  HoleCutDiameter = 0
  HoleCutType = 0
  ModelThread = false
  Profile = -> Pocket036 [Edge26,Edge27]
  Refine = true
  Suppressed = false
  Tapered = false
  TaperedAngle = 90
  ThreadClass = 0
  ThreadDepth = 25
  ThreadDepthType = 0
  ThreadDiameter = 4.5
  ThreadDirection = 0
  ThreadFit = 0
  ThreadSize = 12
  ThreadType = 1
  Threaded = true
  UseCustomThreadClearance = false
FEATURE [PartDesign::Fillet] Fillet028
  Base = -> Hole015 [Edge32,Edge29,Edge31,Edge50,Edge48,Edge34,Edge46,Edge36,Edge38,Edge40,Edge42,Edge44,Edge14,Edge49,Edge8,Edge37,Edge9,Edge13,Edge10,Edge12]
  BaseFeature = -> Hole015
  Radius = 1
  Refine = true
  SupportTransform = false
  Suppressed = false
  UseAllEdges = false
FEATURE [PartDesign::Fillet] Fillet029
  Base = -> Fillet028 [Edge1,Edge27,Edge70]
  BaseFeature = -> Fillet028
  Radius = 0.9
  Refine = true
  SupportTransform = false
  Suppressed = false
  UseAllEdges = false
FEATURE [PartDesign::Fillet] Fillet030
  Base = -> Fillet029 [Face22,Face25]
  BaseFeature = -> Fillet029
  Radius = 0.5
  Refine = true
  SupportTransform = false
  Suppressed = false
  UseAllEdges = false
FEATURE [PartDesign::Fillet] Fillet031
  Base = -> Fillet030 [Face30,Face29]
  BaseFeature = -> Fillet030
  Radius = 1
  Refine = true
  SupportTransform = false
  Suppressed = false
  UseAllEdges = false
FEATURE [PartDesign::Body] Body013  label="RailMount80mm"
  AllowCompound = true
  Group = -> [Sketch047,Pad025,Sketch048,Pocket036,Hole015,Fillet028,Fillet029,Fillet030,Fillet031]
  Origin = -> Origin033
  Tip = -> Fillet031
FEATURE [App::Point] Origin034  label="Origin040"
  Role = Origin
FEATURE [Sketcher::SketchObject] Sketch049  label="SketchPowerDistroBlock002"
  ArcFitTolerance = 1e-06
  AttachmentSupport = -> [Origin035]
  ExternalTypes = [0]
  FullyConstrained = true
  MakeInternals = false
  MapMode = 5
  expr: Constraints[14] = 57 / 2
  expr: Constraints[15] = 57 / 2
  sketch-geometry (9):
    g0: LineSegment StartX=-32.5 StartY=-5 StartZ=0 EndX=32.5 EndY=-5 EndZ=0
    g1: LineSegment StartX=32.5 StartY=-5 StartZ=0 EndX=32.5 EndY=5 EndZ=0
    g2: LineSegment StartX=32.5 StartY=5 StartZ=0 EndX=-32.5 EndY=5 EndZ=0
    g3: LineSegment StartX=-32.5 StartY=5 StartZ=0 EndX=-32.5 EndY=-5 EndZ=0
    g4: GeomPoint [constr] X=0 Y=0 Z=0
    g5: GeomPoint X=-28.5 Y=0 Z=0
    g6: GeomPoint X=28.5 Y=0 Z=0
    g7: Circle CenterX=-28.5 CenterY=0 CenterZ=0 NormalX=0 NormalY=0 NormalZ=1 AngleXU=0 Radius=1.5
    g8: Circle CenterX=28.5 CenterY=0 CenterZ=0 NormalX=0 NormalY=0 NormalZ=1 AngleXU=0 Radius=1.5
  constraints (20):
    c: Coincident(g0,g1)
    c: Coincident(g1,g2)
    c: Coincident(g2,g3)
    c: Coincident(g3,g0)
    c: Horizontal(g0)
    c: Horizontal(g2)
    c: Vertical(g1)
    c: Vertical(g3)
    c: Symmetric(g2,g0,g4)
    c: Distance(g1,g3) = 65
    c: Distance(g0,g2) = 10
    c: Coincident(g4,g-1)
    c: PointOnObject(g5,g-1)
    c: PointOnObject(g6,g-1)
    c: DistanceX(g5,g4) = 28.5
    c: DistanceX(g4,g6) = 28.5
    c: Diameter(g7) = 3
    c: Coincident(g7,g5)
    c: Diameter(g8) = 3
    c: Coincident(g8,g6)
FEATURE [PartDesign::Pad] Pad026
  Direction = (0,0,1)
  Length = 13.6
  Length2 = 10
  Profile = -> Sketch049
  ReferenceAxis = -> Sketch049 [N_Axis]
  Refine = true
  SideType = 0
  Suppressed = false
  Type = 0
  Type2 = 0
  expr: Length = 3 + 5.6 + 3 + 2
FEATURE [Sketcher::SketchObject] Sketch050
  ArcFitTolerance = 1e-06
  AttachmentSupport = -> [Pad026]
  ExternalGeometry = -> [Pad026]
  ExternalTypes = [0]
  FullyConstrained = true
  MakeInternals = false
  MapMode = 5
  Placement = pos=(0,-5,0) rot=(1,0,0;1.5708rad)
  sketch-geometry (27):
    g0: GeomPoint [constr] X=1.7e-15 Y=6.8 Z=0
    g1: LineSegment [constr] StartX=-4.5 StartY=12.6 StartZ=0 EndX=-4.5 EndY=9.6 EndZ=0
    g2: LineSegment [constr] StartX=-4.5 StartY=9.6 StartZ=0 EndX=4.5 EndY=9.6 EndZ=0
    g3: LineSegment [constr] StartX=4.5 StartY=9.6 StartZ=0 EndX=4.5 EndY=12.6 EndZ=0
    g4: LineSegment [constr] StartX=4.5 StartY=12.6 StartZ=0 EndX=-4.5 EndY=12.6 EndZ=0
    g5: LineSegment [constr] StartX=1.5 StartY=9.6 StartZ=0 EndX=1.5 EndY=4 EndZ=0
    g6: LineSegment [constr] StartX=1.5 StartY=4 StartZ=0 EndX=-1.5 EndY=4 EndZ=0
    g7: LineSegment [constr] StartX=-1.5 StartY=4 StartZ=0 EndX=-1.5 EndY=9.6 EndZ=0
    g8: LineSegment [constr] StartX=-1.5 StartY=9.6 StartZ=0 EndX=1.5 EndY=9.6 EndZ=0
    g9: LineSegment [constr] StartX=-4.5 StartY=4 StartZ=0 EndX=-4.5 EndY=1 EndZ=0
    g10: LineSegment [constr] StartX=-4.5 StartY=1 StartZ=0 EndX=4.5 EndY=1 EndZ=0
    g11: LineSegment [constr] StartX=4.5 StartY=1 StartZ=0 EndX=4.5 EndY=4 EndZ=0
    g12: LineSegment [constr] StartX=4.5 StartY=4 StartZ=0 EndX=-4.5 EndY=4 EndZ=0
    g13: GeomPoint [constr] X=2.1e-15 Y=9.6 Z=0
    g14: GeomPoint [constr] X=2.1e-15 Y=4 Z=0
    g15: LineSegment StartX=-4.5 StartY=12.6 StartZ=0 EndX=4.5 EndY=12.6 EndZ=0
    g16: LineSegment StartX=4.5 StartY=12.6 StartZ=0 EndX=4.5 EndY=9.6 EndZ=0
    g17: LineSegment StartX=4.5 StartY=9.6 StartZ=0 EndX=1.5 EndY=9.6 EndZ=0
    g18: LineSegment StartX=1.5 StartY=9.6 StartZ=0 EndX=1.5 EndY=4 EndZ=0
    g19: LineSegment StartX=1.5 StartY=4 StartZ=0 EndX=4.5 EndY=4 EndZ=0
    g20: LineSegment StartX=4.5 StartY=4 StartZ=0 EndX=4.5 EndY=1 EndZ=0
    g21: LineSegment StartX=4.5 StartY=1 StartZ=0 EndX=-4.5 EndY=1 EndZ=0
    g22: LineSegment StartX=-4.5 StartY=1 StartZ=0 EndX=-4.5 EndY=4 EndZ=0
    g23: LineSegment StartX=-4.5 StartY=4 StartZ=0 EndX=-1.5 EndY=4 EndZ=0
    g24: LineSegment StartX=-1.5 StartY=4 StartZ=0 EndX=-1.5 EndY=9.6 EndZ=0
    g25: LineSegment StartX=-1.5 StartY=9.6 StartZ=0 EndX=-4.5 EndY=9.6 EndZ=0
    g26: LineSegment StartX=-4.5 StartY=9.6 StartZ=0 EndX=-4.5 EndY=12.6 EndZ=0
  constraints (60):
    c: Symmetric(g-5,g-6,g0)
    c: Coincident(g1,g2)
    c: Coincident(g2,g3)
    c: Coincident(g3,g4)
    c: Coincident(g4,g1)
    c: Vertical(g1)
    c: Vertical(g3)
    c: Horizontal(g2)
    c: Horizontal(g4)
    c: Distance(g1,g3) = 9
    c: Distance(g2,g4) = 3
    c: Coincident(g5,g6)
    c: Coincident(g6,g7)
    c: Coincident(g7,g8)
    c: Coincident(g8,g5)
    c: Vertical(g5)
    c: Vertical(g7)
    c: Horizontal(g6)
    c: Horizontal(g8)
    c: Distance(g5,g7) = 3
    c: Distance(g6,g8) = 5.6
    c: Coincident(g9,g10)
    c: Coincident(g10,g11)
    c: Coincident(g11,g12)
    c: Coincident(g12,g9)
    c: Vertical(g9)
    c: Vertical(g11)
    c: Horizontal(g10)
    c: Horizontal(g12)
    c: Distance(g9,g11) = 9
    c: Distance(g10,g12) = 3
    c: Symmetric(g1,g2,g13)
    c: Symmetric(g5,g7,g13)
    c: Symmetric(g9,g11,g14)
    c: Symmetric(g5,g6,g14)
    c: Symmetric(g5,g7,g0)
    c: Coincident(g15,g1)
    c: Coincident(g15,g3)
    c: Coincident(g16,g3)
    c: Coincident(g16,g2)
    c: Coincident(g17,g2)
    c: Coincident(g17,g5)
    c: Coincident(g18,g5)
    c: Coincident(g18,g5)
    c: Coincident(g19,g5)
    c: Coincident(g19,g11)
    c: Coincident(g20,g11)
    c: Coincident(g20,g10)
    c: Coincident(g21,g10)
    c: Coincident(g21,g9)
    c: Coincident(g22,g9)
    c: Coincident(g22,g9)
    c: Coincident(g23,g9)
    c: Coincident(g23,g6)
    c: Coincident(g24,g6)
    c: Coincident(g24,g7)
    c: Coincident(g25,g7)
    c: Coincident(g25,g1)
    c: Coincident(g26,g1)
    c: Coincident(g26,g1)
FEATURE [PartDesign::Pocket] Pocket037
  BaseFeature = -> Pad026
  Direction = (0,1,-2e-16)
  Length = 5
  Length2 = 5
  Profile = -> Sketch050
  ReferenceAxis = -> Sketch050 [N_Axis]
  Refine = true
  SideType = 0
  Suppressed = false
  Type = 1
  Type2 = 0
FEATURE [PartDesign::Hole] Hole016
  BaseFeature = -> Pocket037
  BaseProfileType = 7
  CustomThreadClearance = 0
  Depth = 25
  DepthType = 0
  Diameter = 2.9
  DrillForDepth = false
  DrillPoint = 1
  DrillPointAngle = 118
  HoleCutCountersinkAngle = 90
  HoleCutCustomValues = false
  HoleCutDepth = 0
  HoleCutDiameter = 0
  HoleCutType = 0
  ModelThread = false
  Profile = -> Pocket037 [Edge26,Edge27]
  Refine = true
  Suppressed = false
  Tapered = false
  TaperedAngle = 90
  ThreadClass = 0
  ThreadDepth = 25
  ThreadDepthType = 0
  ThreadDiameter = 3.5
  ThreadDirection = 0
  ThreadFit = 0
  ThreadSize = 10
  ThreadType = 1
  Threaded = true
  UseCustomThreadClearance = false
FEATURE [PartDesign::Fillet] Fillet032
  Base = -> Hole016 [Edge32,Edge29,Edge31,Edge50,Edge48,Edge34,Edge46,Edge36,Edge38,Edge40,Edge42,Edge44,Edge14,Edge49,Edge8,Edge37,Edge9,Edge13,Edge10,Edge12]
  BaseFeature = -> Hole016
  Radius = 1
  Refine = true
  SupportTransform = false
  Suppressed = false
  UseAllEdges = false
FEATURE [PartDesign::Fillet] Fillet033
  Base = -> Fillet032 [Edge1,Edge27,Edge70]
  BaseFeature = -> Fillet032
  Radius = 0.9
  Refine = true
  SupportTransform = false
  Suppressed = false
  UseAllEdges = false
FEATURE [PartDesign::Fillet] Fillet034
  Base = -> Fillet033 [Face22,Face25]
  BaseFeature = -> Fillet033
  Radius = 0.5
  Refine = true
  SupportTransform = false
  Suppressed = false
  UseAllEdges = false
FEATURE [PartDesign::Fillet] Fillet035
  Base = -> Fillet034 [Face30,Face29]
  BaseFeature = -> Fillet034
  Radius = 1
  Refine = true
  SupportTransform = false
  Suppressed = false
  UseAllEdges = false
FEATURE [PartDesign::Body] Body014  label="RailMount57mm"
  AllowCompound = true
  Group = -> [Sketch049,Pad026,Sketch050,Pocket037,Hole016,Fillet032,Fillet033,Fillet034,Fillet035]
  Origin = -> Origin035
  Tip = -> Fillet035
FEATURE [PartDesign::Pad] Pad
  BaseFeature = -> Pocket001
  Direction = (0,1,0)
  Length = 10
  Length2 = 10
  Profile = -> Pocket001 [Face6]
  Refine = true
  SideType = 0
  Suppressed = false
  Type = 0
  Type2 = 0
FEATURE [Sketcher::SketchObject] Sketch051
  ArcFitTolerance = 1e-06
  AttachmentSupport = -> [Pad]
  ExternalGeometry = -> [Pad,Sketch020]
  ExternalTypes = [0,0,0]
  FullyConstrained = true
  MakeInternals = false
  MapMode = 5
  Placement = pos=(10,0,0) rot=(0.57735,0.57735,0.57735;2.0944rad)
  sketch-geometry (7):
    g0: LineSegment [constr] StartX=1 StartY=0 StartZ=0 EndX=11 EndY=0 EndZ=0
    g1: LineSegment [constr] StartX=11 StartY=0 StartZ=0 EndX=11 EndY=10 EndZ=0
    g2: LineSegment [constr] StartX=11 StartY=10 StartZ=0 EndX=1 EndY=10 EndZ=0
    g3: LineSegment [constr] StartX=1 StartY=10 StartZ=0 EndX=1 EndY=0 EndZ=0
    g4: LineSegment StartX=1 StartY=10 StartZ=0 EndX=11 EndY=0 EndZ=0
    g5: LineSegment StartX=11 StartY=0 StartZ=0 EndX=11 EndY=10 EndZ=0
    g6: LineSegment StartX=11 StartY=10 StartZ=0 EndX=1 EndY=10 EndZ=0
  constraints (16):
    c: Coincident(g0,g1)
    c: Coincident(g1,g2)
    c: Coincident(g2,g3)
    c: Coincident(g3,g0)
    c: Horizontal(g0)
    c: Horizontal(g2)
    c: Vertical(g1)
    c: Vertical(g3)
    c: Coincident(g0,g-20)
    c: Coincident(g1,g-7)
    c: Coincident(g4,g2)
    c: Coincident(g4,g0)
    c: Coincident(g5,g0)
    c: Coincident(g5,g1)
    c: Coincident(g6,g1)
    c: Coincident(g6,g2)
FEATURE [PartDesign::Pocket] Pocket038
  BaseFeature = -> Pad
  Direction = (-1,0,0)
  Length = 5
  Length2 = 5
  Profile = -> Sketch051
  ReferenceAxis = -> Sketch051 [N_Axis]
  Refine = true
  SideType = 0
  Suppressed = false
  Type = 1
  Type2 = 0
FEATURE [PartDesign::Fillet] Fillet036
  Base = -> Pocket038 [Edge64,Edge66,Edge68,Edge71,Edge73,Edge75,Edge70,Edge72,Edge65,Edge67,Edge69,Edge74,Edge105,Edge109,Edge107,Edge103,Edge100,Edge101,Edge111,Edge115,Edge113,Edge117,Edge119,Edge121,Edge97,Edge95,Edge91,Edge87,Edge89,Edge93,Edge83,Edge85,Edge81,Edge79,Edge76,Edge77]
  BaseFeature = -> Pocket038
  Radius = 1
  Refine = true
  SupportTransform = false
  Suppressed = false
  UseAllEdges = false
FEATURE [PartDesign::Fillet] Fillet037
  Base = -> Fillet036 [Edge1,Edge2,Edge3,Edge4,Edge5,Edge6,Edge7,Edge8,Edge9,Edge10,Edge11,Edge12,Edge13,Edge14,Edge15,Edge16,Edge17,Edge18,Edge19,Edge20,Edge21,Edge22,Edge23,Edge24,Edge25,Edge26,Edge27,Edge28,Edge29,Edge30,Edge31,Edge32,Edge33,Edge34,Edge35,Edge36,Edge37,Edge38,Edge39,Edge40,+191 more]
  BaseFeature = -> Fillet036
  Radius = 0.45
  Refine = true
  SupportTransform = false
  Suppressed = false
  UseAllEdges = true
FEATURE [PartDesign::Body] Body007  label="ConnectorSlidingL"
  AllowCompound = true
  Group = -> [Binder012,Sketch018,Pad021,Sketch019,Pad022,Sketch020,Pad023,Sketch021,Pocket001,Pad,Sketch051,Pocket038,Fillet036,Fillet037]
  Origin = -> Origin028
  Tip = -> Fillet037
